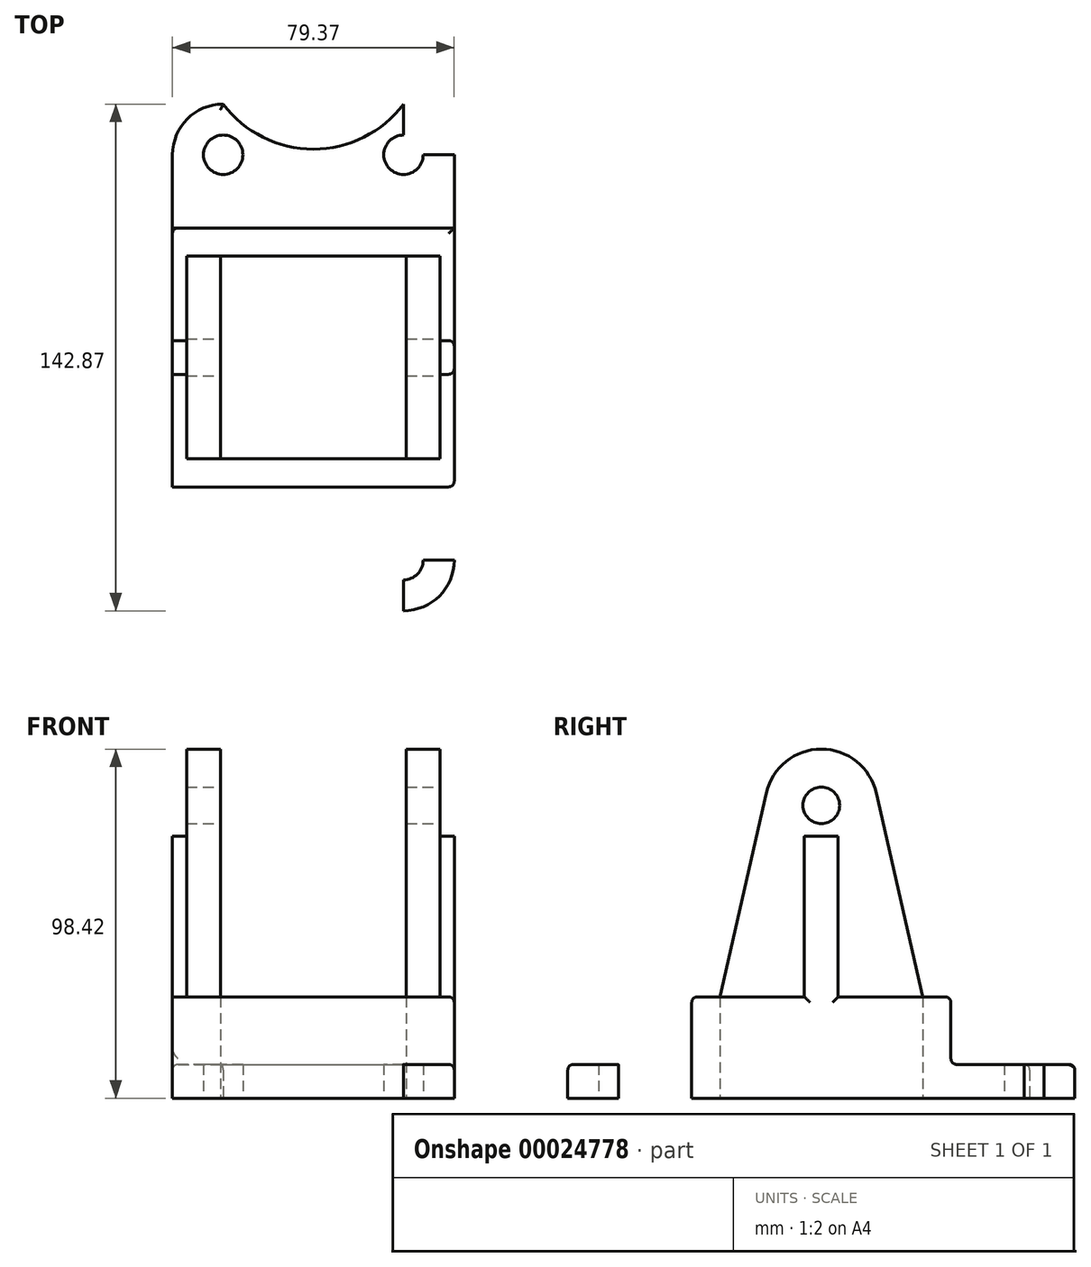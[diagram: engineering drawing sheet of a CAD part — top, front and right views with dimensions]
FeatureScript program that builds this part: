
annotation { "Feature Type Name" : "Feature", "Feature Type Description" : "" }
export const myFeature = defineFeature(function(context is Context, id is Id, definition is map)
    precondition{}
    {
        {
            var Q0;
            Q0=qCreatedBy(makeId("Top.planeOp"),FACE);
            var sketch = newSketch(context, id + "F0", { "sketchPlane" : qUnion([Q0])});
            skArc(sketch, "E0", {"start": v(-23.97, 73.31) * mm, "mid": v(-34.08, 69.13) * mm, "end": v(-38.26, 59.03) * mm});
            skLineSegment(sketch, "E1", {"start": v(-23.97, 59.03) * mm, "end": v(-23.97, 73.31) * mm, "construction": true});
            skLineSegment(sketch, "E2", {"start": v(-23.97, 59.03) * mm, "end": v(-38.26, 59.03) * mm, "construction": true});
            skLineSegment(sketch, "E3", {"start": v(-38.26, 59.03) * mm, "end": v(-38.26, -55.27) * mm});
            skLineSegment(sketch, "E4", {"start": v(-23.97, 73.31) * mm, "end": v(26.83, 73.31) * mm, "construction": true});
            skPoint(sketch, "E5", {"position": v(1.43, 73.31) * mm});
            skArc(sketch, "E6", {"start": v(-23.97, 73.31) * mm, "mid": v(1.43, 60.61) * mm, "end": v(26.83, 73.31) * mm});
            skCircle(sketch, "E7", {"center": v(-23.97, 59.03) * mm, "radius": 5.56 * mm});
            skPoint(sketch, "E8", {"position": v(-38.26, 1.88) * mm});
            skLineSegment(sketch, "E9.MirrorCS", {"start": v(-23.97, -69.56) * mm, "end": v(26.83, -69.56) * mm, "construction": true});
            skArc(sketch, "E10.MirrorCS", {"start": v(-23.97, -69.56) * mm, "mid": v(1.43, -56.86) * mm, "end": v(26.83, -69.56) * mm});
            skArc(sketch, "E11.MirrorC", {"start": v(-23.97, -69.56) * mm, "mid": v(-34.08, -65.38) * mm, "end": v(-38.26, -55.27) * mm});
            skLineSegment(sketch, "E12.MirrorCS", {"start": v(-23.97, -55.27) * mm, "end": v(-38.26, -55.27) * mm, "construction": true});
            skCircle(sketch, "E13.MirrorC", {"center": v(-23.97, -55.27) * mm, "radius": 5.56 * mm});
            skLineSegment(sketch, "E14.MirrorCS", {"start": v(-23.97, -55.27) * mm, "end": v(-23.97, -69.56) * mm, "construction": true});
            skPoint(sketch, "E15.MirrorP", {"position": v(1.43, -69.56) * mm});
            skLineSegment(sketch, "E16", {"start": v(-38.26, 1.88) * mm, "end": v(-34.3, 1.88) * mm, "construction": true});
            skLineSegment(sketch, "E17", {"start": v(-34.3, 6.64) * mm, "end": v(-34.3, -2.89) * mm});
            skPoint(sketch, "E18", {"position": v(-34.3, 1.88) * mm});
            skLineSegment(sketch, "E19", {"start": v(-34.3, 6.64) * mm, "end": v(-38.26, 6.64) * mm});
            skLineSegment(sketch, "E20", {"start": v(-34.3, -2.89) * mm, "end": v(-38.26, -2.89) * mm});
            skLineSegment(sketch, "E21", {"start": v(1.43, 73.31) * mm, "end": v(1.43, -69.56) * mm, "construction": true});
            skLineSegment(sketch, "E22", {"start": v(-34.3, 1.88) * mm, "end": v(-34.3, 30.45) * mm, "construction": true});
            skLineSegment(sketch, "E23", {"start": v(-38.26, 30.45) * mm, "end": v(1.43, 30.45) * mm});
            skLineSegment(sketch, "E24", {"start": v(-38.26, 38.39) * mm, "end": v(1.43, 38.39) * mm});
            skLineSegment(sketch, "E25.MirrorCS", {"start": v(37.14, -2.89) * mm, "end": v(41.11, -2.89) * mm});
            skLineSegment(sketch, "E26.MirrorCS", {"start": v(41.11, 1.88) * mm, "end": v(37.14, 1.88) * mm, "construction": true});
            skLineSegment(sketch, "E27.MirrorCS", {"start": v(37.14, 6.64) * mm, "end": v(37.14, -2.89) * mm});
            skLineSegment(sketch, "E28.MirrorCS", {"start": v(37.14, 6.64) * mm, "end": v(41.11, 6.64) * mm});
            skLineSegment(sketch, "E29.MirrorCS", {"start": v(37.14, 1.88) * mm, "end": v(37.14, 30.45) * mm, "construction": true});
            skCircle(sketch, "E30.MirrorC", {"center": v(26.83, -55.27) * mm, "radius": 5.56 * mm});
            skLineSegment(sketch, "E31.MirrorCS", {"start": v(26.83, -55.27) * mm, "end": v(41.11, -55.27) * mm});
            skLineSegment(sketch, "E32.MirrorCS", {"start": v(41.11, 38.39) * mm, "end": v(1.43, 38.39) * mm});
            skCircle(sketch, "E33.MirrorC", {"center": v(26.83, 59.03) * mm, "radius": 5.56 * mm});
            skArc(sketch, "E34.MirrorCS", {"start": v(26.83, -69.56) * mm, "mid": v(36.93, -65.38) * mm, "end": v(41.11, -55.27) * mm});
            skLineSegment(sketch, "E35.MirrorCS", {"start": v(41.11, 30.45) * mm, "end": v(1.43, 30.45) * mm});
            skPoint(sketch, "E36.MirrorP", {"position": v(41.11, 1.88) * mm});
            skLineSegment(sketch, "E37.MirrorCS", {"start": v(26.83, -55.27) * mm, "end": v(26.83, -69.56) * mm});
            skPoint(sketch, "E38.MirrorP", {"position": v(37.14, 1.88) * mm});
            skArc(sketch, "E39.MirrorCS", {"start": v(26.83, 73.31) * mm, "mid": v(36.93, 69.13) * mm, "end": v(41.11, 59.03) * mm});
            skLineSegment(sketch, "E40.MirrorCS", {"start": v(26.83, 59.03) * mm, "end": v(26.83, 73.31) * mm});
            skLineSegment(sketch, "E41.MirrorCS", {"start": v(26.83, 59.03) * mm, "end": v(41.11, 59.03) * mm});
            skLineSegment(sketch, "E42.MirrorCS", {"start": v(41.11, 59.03) * mm, "end": v(41.11, -55.27) * mm});
            skLineSegment(sketch, "E43", {"start": v(-34.3, -2.89) * mm, "end": v(-34.3, -26.7) * mm, "construction": true});
            skLineSegment(sketch, "E44", {"start": v(-38.26, -26.7) * mm, "end": v(41.11, -26.7) * mm});
            skLineSegment(sketch, "E45", {"start": v(-38.26, -34.64) * mm, "end": v(41.11, -34.64) * mm});
            skLineSegment(sketch, "E46", {"start": v(-34.3, 38.39) * mm, "end": v(-34.3, -34.64) * mm});
            skLineSegment(sketch, "E47", {"start": v(-24.77, 38.39) * mm, "end": v(-24.77, -34.64) * mm});
            skLineSegment(sketch, "E48", {"start": v(37.14, 38.39) * mm, "end": v(37.14, -34.64) * mm});
            skLineSegment(sketch, "E49", {"start": v(27.62, 38.39) * mm, "end": v(27.62, -34.64) * mm});
            skSolve(sketch);
        }
        {
            var Q0;
            {var subQ1=sQuery(id+"F0.wireOp",EDGE,"E23");var subQ5=sQuery(id+"F0.wireOp",EDGE,"E3");var subQ7=makeQuery(id+"F0.imprint","INTERSECT",VERTEX,{"derivedFrom":[subQ5,subQ1]});Q0=makeQuery(id+"F0.imprint","IMPRINT",FACE,{"disambiguationData":[TD([[makeQuery(id+"F0.imprint","IMPRINT",EDGE,{"disambiguationData":[TD([[subQ7,1.0]])],"derivedFrom":subQ5}),1.0]])]});}
            var Q1;
            {var subQ5=sQuery(id+"F0.wireOp",EDGE,"E19");Q1=makeQuery(id+"F0.imprint","IMPRINT",FACE,{"disambiguationData":[TD([[makeQuery(id+"F0.imprint","IMPRINT",EDGE,{"derivedFrom":subQ5}),-1.0]])]});}
            var Q2;
            {var subQ3=sQuery(id+"F0.wireOp",EDGE,"E35.MirrorCS");var subQ7=sQuery(id+"F0.wireOp",EDGE,"E23");var subQ9=makeQuery(id+"F0.imprint","INTERSECT",VERTEX,{"derivedFrom":[subQ7,subQ3]});Q2=makeQuery(id+"F0.imprint","IMPRINT",FACE,{"disambiguationData":[TD([[makeQuery(id+"F0.imprint","IMPRINT",EDGE,{"disambiguationData":[TD([[subQ9,1.0]])],"derivedFrom":subQ7}),-1.0]])]});}
            var Q3;
            {var subQ3=sQuery(id+"F0.wireOp",EDGE,"E25.MirrorCS");Q3=makeQuery(id+"F0.imprint","IMPRINT",FACE,{"disambiguationData":[TD([[makeQuery(id+"F0.imprint","IMPRINT",EDGE,{"derivedFrom":subQ3}),-1.0]])]});}
            var Q4;
            {var subQ3=sQuery(id+"F0.wireOp",EDGE,"E20");Q4=makeQuery(id+"F0.imprint","IMPRINT",FACE,{"disambiguationData":[TD([[makeQuery(id+"F0.imprint","IMPRINT",EDGE,{"derivedFrom":subQ3}),1.0]])]});}
            var Q5;
            {var subQ1=sQuery(id+"F0.wireOp",EDGE,"E44");var subQ5=sQuery(id+"F0.wireOp",EDGE,"E3");var subQ7=makeQuery(id+"F0.imprint","INTERSECT",VERTEX,{"derivedFrom":[subQ5,subQ1]});Q5=makeQuery(id+"F0.imprint","IMPRINT",FACE,{"disambiguationData":[TD([[makeQuery(id+"F0.imprint","IMPRINT",EDGE,{"disambiguationData":[TD([[subQ7,-1.0]])],"derivedFrom":subQ5}),1.0]])]});}
            var Q6;
            {var subQ3=sQuery(id+"F0.wireOp",EDGE,"E28.MirrorCS");Q6=makeQuery(id+"F0.imprint","IMPRINT",FACE,{"disambiguationData":[TD([[makeQuery(id+"F0.imprint","IMPRINT",EDGE,{"derivedFrom":subQ3}),1.0]])]});}
            var Q7;
            {var subQ0=sQuery(id+"F0.wireOp",EDGE,"E42.MirrorCS");var subQ3=sQuery(id+"F0.wireOp",EDGE,"E32.MirrorCS");var subQ4=makeQuery(id+"F0.imprint","INTERSECT",VERTEX,{"derivedFrom":[subQ3,subQ0]});Q7=makeQuery(id+"F0.imprint","IMPRINT",FACE,{"disambiguationData":[TD([[makeQuery(id+"F0.imprint","IMPRINT",EDGE,{"disambiguationData":[TD([[subQ4,-1.0]])],"derivedFrom":subQ3}),1.0]])]});}
            var Q8;
            {var subQ1=sQuery(id+"F0.wireOp",EDGE,"E44");var subQ5=sQuery(id+"F0.wireOp",EDGE,"E46");var subQ6=makeQuery(id+"F0.imprint","INTERSECT",VERTEX,{"derivedFrom":[subQ1,subQ5]});Q8=makeQuery(id+"F0.imprint","IMPRINT",FACE,{"disambiguationData":[TD([[makeQuery(id+"F0.imprint","IMPRINT",EDGE,{"disambiguationData":[TD([[subQ6,-1.0]])],"derivedFrom":subQ1}),-1.0]])]});}
            var Q9;
            {var subQ1=sQuery(id+"F0.wireOp",EDGE,"E44");var subQ5=sQuery(id+"F0.wireOp",EDGE,"E47");var subQ6=makeQuery(id+"F0.imprint","INTERSECT",VERTEX,{"derivedFrom":[subQ1,subQ5]});Q9=makeQuery(id+"F0.imprint","IMPRINT",FACE,{"disambiguationData":[TD([[makeQuery(id+"F0.imprint","IMPRINT",EDGE,{"disambiguationData":[TD([[subQ6,-1.0]])],"derivedFrom":subQ1}),-1.0]])]});}
            var Q10;
            {var subQ3=sQuery(id+"F0.wireOp",EDGE,"E32.MirrorCS");var subQ5=sQuery(id+"F0.wireOp",EDGE,"E48");var subQ7=makeQuery(id+"F0.imprint","INTERSECT",VERTEX,{"derivedFrom":[subQ3,subQ5]});Q10=makeQuery(id+"F0.imprint","IMPRINT",FACE,{"disambiguationData":[TD([[makeQuery(id+"F0.imprint","IMPRINT",EDGE,{"disambiguationData":[TD([[subQ7,-1.0]])],"derivedFrom":subQ3}),1.0]])]});}
            var Q11;
            {var subQ3=sQuery(id+"F0.wireOp",EDGE,"E42.MirrorCS");var subQ5=sQuery(id+"F0.wireOp",EDGE,"E44");var subQ7=makeQuery(id+"F0.imprint","INTERSECT",VERTEX,{"derivedFrom":[subQ3,subQ5]});Q11=makeQuery(id+"F0.imprint","IMPRINT",FACE,{"disambiguationData":[TD([[makeQuery(id+"F0.imprint","IMPRINT",EDGE,{"disambiguationData":[TD([[subQ7,-1.0]])],"derivedFrom":subQ3}),-1.0]])]});}
            var Q12;
            {var subQ0=sQuery(id+"F0.wireOp",EDGE,"E49");var subQ1=sQuery(id+"F0.wireOp",EDGE,"E44");var subQ2=makeQuery(id+"F0.imprint","INTERSECT",VERTEX,{"derivedFrom":[subQ1,subQ0]});Q12=makeQuery(id+"F0.imprint","IMPRINT",FACE,{"disambiguationData":[TD([[makeQuery(id+"F0.imprint","IMPRINT",EDGE,{"disambiguationData":[TD([[subQ2,-1.0]])],"derivedFrom":subQ1}),-1.0]])]});}
            var Q13;
            {var subQ1=sQuery(id+"F0.wireOp",EDGE,"E23");var subQ5=sQuery(id+"F0.wireOp",EDGE,"E46");var subQ6=makeQuery(id+"F0.imprint","INTERSECT",VERTEX,{"derivedFrom":[subQ1,subQ5]});Q13=makeQuery(id+"F0.imprint","IMPRINT",FACE,{"disambiguationData":[TD([[makeQuery(id+"F0.imprint","IMPRINT",EDGE,{"disambiguationData":[TD([[subQ6,-1.0]])],"derivedFrom":subQ1}),1.0]])]});}
            var Q14;
            {var subQ3=sQuery(id+"F0.wireOp",EDGE,"E35.MirrorCS");var subQ5=sQuery(id+"F0.wireOp",EDGE,"E48");var subQ9=makeQuery(id+"F0.imprint","INTERSECT",VERTEX,{"derivedFrom":[subQ3,subQ5]});Q14=makeQuery(id+"F0.imprint","IMPRINT",FACE,{"disambiguationData":[TD([[makeQuery(id+"F0.imprint","IMPRINT",EDGE,{"disambiguationData":[TD([[subQ9,-1.0]])],"derivedFrom":subQ3}),1.0]])]});}
            var Q15;
            {var subQ3=sQuery(id+"F0.wireOp",EDGE,"E23");var subQ5=sQuery(id+"F0.wireOp",EDGE,"E46");var subQ9=makeQuery(id+"F0.imprint","INTERSECT",VERTEX,{"derivedFrom":[subQ3,subQ5]});Q15=makeQuery(id+"F0.imprint","IMPRINT",FACE,{"disambiguationData":[TD([[makeQuery(id+"F0.imprint","IMPRINT",EDGE,{"disambiguationData":[TD([[subQ9,-1.0]])],"derivedFrom":subQ3}),-1.0]])]});}
            var Q16;
            {var subQ1=sQuery(id+"F0.wireOp",EDGE,"E35.MirrorCS");var subQ6=sQuery(id+"F0.wireOp",EDGE,"E23");var subQ10=makeQuery(id+"F0.imprint","INTERSECT",VERTEX,{"derivedFrom":[subQ6,subQ1]});Q16=makeQuery(id+"F0.imprint","IMPRINT",FACE,{"disambiguationData":[TD([[makeQuery(id+"F0.imprint","IMPRINT",EDGE,{"disambiguationData":[TD([[subQ10,1.0]])],"derivedFrom":subQ6}),1.0]])]});}
            var Q17;
            {var subQ19=sQuery(id+"F0.wireOp",EDGE,"E0");Q17=makeQuery(id+"F0.imprint","IMPRINT",FACE,{"disambiguationData":[TD([[makeQuery(id+"F0.imprint","IMPRINT",EDGE,{"derivedFrom":subQ19}),1.0]])]});}
            var Q18;
            {var subQ3=sQuery(id+"F0.wireOp",EDGE,"E39.MirrorCS");Q18=makeQuery(id+"F0.imprint","IMPRINT",FACE,{"disambiguationData":[TD([[makeQuery(id+"F0.imprint","IMPRINT",EDGE,{"derivedFrom":subQ3}),-1.0]])]});}
            var Q19;
            {var subQ10=sQuery(id+"F0.wireOp",EDGE,"E10.MirrorCS");Q19=makeQuery(id+"F0.imprint","IMPRINT",FACE,{"disambiguationData":[TD([[makeQuery(id+"F0.imprint","IMPRINT",EDGE,{"derivedFrom":subQ10}),1.0]])]});}
            var Q20;
            {var subQ3=sQuery(id+"F0.wireOp",EDGE,"E34.MirrorCS");Q20=makeQuery(id+"F0.imprint","IMPRINT",FACE,{"disambiguationData":[TD([[makeQuery(id+"F0.imprint","IMPRINT",EDGE,{"derivedFrom":subQ3}),1.0]])]});}
            extrude(context, id + "F1", {"entities" : qUnion([Q0, Q1, Q2, Q3, Q4, Q5, Q6, Q7, Q8, Q9, Q10, Q11, Q12, Q13, Q14, Q15, Q16, Q17, Q18, Q19, Q20]), "depth" : 9.52 * mm});
        }
        {
            var Q0;
            {var subQ0=sQuery(id+"F0.wireOp",EDGE,"E42.MirrorCS");var subQ3=sQuery(id+"F0.wireOp",EDGE,"E32.MirrorCS");var subQ4=makeQuery(id+"F0.imprint","INTERSECT",VERTEX,{"derivedFrom":[subQ3,subQ0]});Q0=makeQuery(id+"F0.imprint","IMPRINT",FACE,{"disambiguationData":[TD([[makeQuery(id+"F0.imprint","IMPRINT",EDGE,{"disambiguationData":[TD([[subQ4,-1.0]])],"derivedFrom":subQ3}),1.0]])]});}
            var Q1;
            {var subQ3=sQuery(id+"F0.wireOp",EDGE,"E32.MirrorCS");var subQ5=sQuery(id+"F0.wireOp",EDGE,"E48");var subQ7=makeQuery(id+"F0.imprint","INTERSECT",VERTEX,{"derivedFrom":[subQ3,subQ5]});Q1=makeQuery(id+"F0.imprint","IMPRINT",FACE,{"disambiguationData":[TD([[makeQuery(id+"F0.imprint","IMPRINT",EDGE,{"disambiguationData":[TD([[subQ7,-1.0]])],"derivedFrom":subQ3}),1.0]])]});}
            var Q2;
            {var subQ1=sQuery(id+"F0.wireOp",EDGE,"E35.MirrorCS");var subQ6=sQuery(id+"F0.wireOp",EDGE,"E23");var subQ10=makeQuery(id+"F0.imprint","INTERSECT",VERTEX,{"derivedFrom":[subQ6,subQ1]});Q2=makeQuery(id+"F0.imprint","IMPRINT",FACE,{"disambiguationData":[TD([[makeQuery(id+"F0.imprint","IMPRINT",EDGE,{"disambiguationData":[TD([[subQ10,1.0]])],"derivedFrom":subQ6}),1.0]])]});}
            var Q3;
            {var subQ1=sQuery(id+"F0.wireOp",EDGE,"E23");var subQ5=sQuery(id+"F0.wireOp",EDGE,"E46");var subQ6=makeQuery(id+"F0.imprint","INTERSECT",VERTEX,{"derivedFrom":[subQ1,subQ5]});Q3=makeQuery(id+"F0.imprint","IMPRINT",FACE,{"disambiguationData":[TD([[makeQuery(id+"F0.imprint","IMPRINT",EDGE,{"disambiguationData":[TD([[subQ6,-1.0]])],"derivedFrom":subQ1}),1.0]])]});}
            var Q4;
            {var subQ1=sQuery(id+"F0.wireOp",EDGE,"E23");var subQ5=sQuery(id+"F0.wireOp",EDGE,"E3");var subQ7=makeQuery(id+"F0.imprint","INTERSECT",VERTEX,{"derivedFrom":[subQ5,subQ1]});Q4=makeQuery(id+"F0.imprint","IMPRINT",FACE,{"disambiguationData":[TD([[makeQuery(id+"F0.imprint","IMPRINT",EDGE,{"disambiguationData":[TD([[subQ7,1.0]])],"derivedFrom":subQ5}),1.0]])]});}
            var Q5;
            {var subQ3=sQuery(id+"F0.wireOp",EDGE,"E42.MirrorCS");var subQ5=sQuery(id+"F0.wireOp",EDGE,"E44");var subQ7=makeQuery(id+"F0.imprint","INTERSECT",VERTEX,{"derivedFrom":[subQ3,subQ5]});Q5=makeQuery(id+"F0.imprint","IMPRINT",FACE,{"disambiguationData":[TD([[makeQuery(id+"F0.imprint","IMPRINT",EDGE,{"disambiguationData":[TD([[subQ7,-1.0]])],"derivedFrom":subQ3}),-1.0]])]});}
            var Q6;
            {var subQ0=sQuery(id+"F0.wireOp",EDGE,"E49");var subQ1=sQuery(id+"F0.wireOp",EDGE,"E44");var subQ2=makeQuery(id+"F0.imprint","INTERSECT",VERTEX,{"derivedFrom":[subQ1,subQ0]});Q6=makeQuery(id+"F0.imprint","IMPRINT",FACE,{"disambiguationData":[TD([[makeQuery(id+"F0.imprint","IMPRINT",EDGE,{"disambiguationData":[TD([[subQ2,-1.0]])],"derivedFrom":subQ1}),-1.0]])]});}
            var Q7;
            {var subQ1=sQuery(id+"F0.wireOp",EDGE,"E44");var subQ5=sQuery(id+"F0.wireOp",EDGE,"E47");var subQ6=makeQuery(id+"F0.imprint","INTERSECT",VERTEX,{"derivedFrom":[subQ1,subQ5]});Q7=makeQuery(id+"F0.imprint","IMPRINT",FACE,{"disambiguationData":[TD([[makeQuery(id+"F0.imprint","IMPRINT",EDGE,{"disambiguationData":[TD([[subQ6,-1.0]])],"derivedFrom":subQ1}),-1.0]])]});}
            var Q8;
            {var subQ1=sQuery(id+"F0.wireOp",EDGE,"E44");var subQ5=sQuery(id+"F0.wireOp",EDGE,"E46");var subQ6=makeQuery(id+"F0.imprint","INTERSECT",VERTEX,{"derivedFrom":[subQ1,subQ5]});Q8=makeQuery(id+"F0.imprint","IMPRINT",FACE,{"disambiguationData":[TD([[makeQuery(id+"F0.imprint","IMPRINT",EDGE,{"disambiguationData":[TD([[subQ6,-1.0]])],"derivedFrom":subQ1}),-1.0]])]});}
            var Q9;
            {var subQ1=sQuery(id+"F0.wireOp",EDGE,"E44");var subQ5=sQuery(id+"F0.wireOp",EDGE,"E3");var subQ7=makeQuery(id+"F0.imprint","INTERSECT",VERTEX,{"derivedFrom":[subQ5,subQ1]});Q9=makeQuery(id+"F0.imprint","IMPRINT",FACE,{"disambiguationData":[TD([[makeQuery(id+"F0.imprint","IMPRINT",EDGE,{"disambiguationData":[TD([[subQ7,-1.0]])],"derivedFrom":subQ5}),1.0]])]});}
            var Q10;
            {var subQ5=sQuery(id+"F0.wireOp",EDGE,"E19");Q10=makeQuery(id+"F0.imprint","IMPRINT",FACE,{"disambiguationData":[TD([[makeQuery(id+"F0.imprint","IMPRINT",EDGE,{"derivedFrom":subQ5}),-1.0]])]});}
            var Q11;
            {var subQ3=sQuery(id+"F0.wireOp",EDGE,"E20");Q11=makeQuery(id+"F0.imprint","IMPRINT",FACE,{"disambiguationData":[TD([[makeQuery(id+"F0.imprint","IMPRINT",EDGE,{"derivedFrom":subQ3}),1.0]])]});}
            var Q12;
            {var subQ3=sQuery(id+"F0.wireOp",EDGE,"E28.MirrorCS");Q12=makeQuery(id+"F0.imprint","IMPRINT",FACE,{"disambiguationData":[TD([[makeQuery(id+"F0.imprint","IMPRINT",EDGE,{"derivedFrom":subQ3}),1.0]])]});}
            var Q13;
            {var subQ3=sQuery(id+"F0.wireOp",EDGE,"E25.MirrorCS");Q13=makeQuery(id+"F0.imprint","IMPRINT",FACE,{"disambiguationData":[TD([[makeQuery(id+"F0.imprint","IMPRINT",EDGE,{"derivedFrom":subQ3}),-1.0]])]});}
            var Q14;
            {var subQ3=sQuery(id+"F0.wireOp",EDGE,"E35.MirrorCS");var subQ5=sQuery(id+"F0.wireOp",EDGE,"E48");var subQ9=makeQuery(id+"F0.imprint","INTERSECT",VERTEX,{"derivedFrom":[subQ3,subQ5]});Q14=makeQuery(id+"F0.imprint","IMPRINT",FACE,{"disambiguationData":[TD([[makeQuery(id+"F0.imprint","IMPRINT",EDGE,{"disambiguationData":[TD([[subQ9,-1.0]])],"derivedFrom":subQ3}),1.0]])]});}
            var Q15;
            {var subQ3=sQuery(id+"F0.wireOp",EDGE,"E23");var subQ5=sQuery(id+"F0.wireOp",EDGE,"E46");var subQ9=makeQuery(id+"F0.imprint","INTERSECT",VERTEX,{"derivedFrom":[subQ3,subQ5]});Q15=makeQuery(id+"F0.imprint","IMPRINT",FACE,{"disambiguationData":[TD([[makeQuery(id+"F0.imprint","IMPRINT",EDGE,{"disambiguationData":[TD([[subQ9,-1.0]])],"derivedFrom":subQ3}),-1.0]])]});}
            extrude(context, id + "F2", {"entities" : qUnion([Q0, Q1, Q2, Q3, Q4, Q5, Q6, Q7, Q8, Q9, Q10, Q11, Q12, Q13, Q14, Q15]), "operationType" : NewBodyOperationType.ADD, "depth" : 28.57 * mm});
        }
        {
            var Q0;
            Q0=makeQuery(id+"F2.boolean.opBoolean","SPLIT",FACE,{"disambiguationData":[TD([makeQuery(id+"F2.opExtrude","SWEPT_FACE",FACE,{"disambiguationData":[OSD([sQuery(id+"F0.wireOp",EDGE,"E44")])]})])],"derivedFrom":makeQuery(id+"F1.opExtrude","CAP_FACE",FACE,{"disambiguationData":[OSD([sQuery(id+"F0.wireOp",EDGE,"E0"),sQuery(id+"F0.wireOp",EDGE,"E3"),sQuery(id+"F0.wireOp",EDGE,"E6"),sQuery(id+"F0.wireOp",EDGE,"E7"),sQuery(id+"F0.wireOp",EDGE,"E10.MirrorCS"),sQuery(id+"F0.wireOp",EDGE,"E11.MirrorC"),sQuery(id+"F0.wireOp",EDGE,"E13.MirrorC"),sQuery(id+"F0.wireOp",EDGE,"E30.MirrorC"),sQuery(id+"F0.wireOp",EDGE,"E33.MirrorC"),sQuery(id+"F0.wireOp",EDGE,"E34.MirrorCS"),sQuery(id+"F0.wireOp",EDGE,"E39.MirrorCS"),sQuery(id+"F0.wireOp",EDGE,"E42.MirrorCS")])],"isStart":false})});
            extrude(context, id + "F3", {"entities" : qUnion([Q0]), "operationType" : NewBodyOperationType.REMOVE, "oppositeDirection" : true, "depth" : 25.4 * mm});
        }
        {
            var Q0;
            {var subQ2=sQuery(id+"F0.wireOp",EDGE,"E19");Q0=makeQuery(id+"F0.imprint","IMPRINT",FACE,{"disambiguationData":[TD([[makeQuery(id+"F0.imprint","IMPRINT",EDGE,{"derivedFrom":subQ2}),1.0]])]});}
            var Q1;
            {var subQ2=sQuery(id+"F0.wireOp",EDGE,"E25.MirrorCS");Q1=makeQuery(id+"F0.imprint","IMPRINT",FACE,{"disambiguationData":[TD([[makeQuery(id+"F0.imprint","IMPRINT",EDGE,{"derivedFrom":subQ2}),1.0]])]});}
            extrude(context, id + "F4", {"entities" : qUnion([Q0, Q1]), "operationType" : NewBodyOperationType.ADD, "depth" : 73.82 * mm});
        }
        {
            var Q0;
            Q0=makeQuery(id+"F2.opExtrude","CAP_FACE",FACE,{"disambiguationData":[OSD([sQuery(id+"F0.wireOp",EDGE,"E3"),sQuery(id+"F0.wireOp",EDGE,"E19"),sQuery(id+"F0.wireOp",EDGE,"E20"),sQuery(id+"F0.wireOp",EDGE,"E23"),sQuery(id+"F0.wireOp",EDGE,"E24"),sQuery(id+"F0.wireOp",EDGE,"E25.MirrorCS"),sQuery(id+"F0.wireOp",EDGE,"E28.MirrorCS"),sQuery(id+"F0.wireOp",EDGE,"E32.MirrorCS"),sQuery(id+"F0.wireOp",EDGE,"E35.MirrorCS"),sQuery(id+"F0.wireOp",EDGE,"E42.MirrorCS"),sQuery(id+"F0.wireOp",EDGE,"E44"),sQuery(id+"F0.wireOp",EDGE,"E45"),sQuery(id+"F0.wireOp",EDGE,"E46"),sQuery(id+"F0.wireOp",EDGE,"E47"),sQuery(id+"F0.wireOp",EDGE,"E48"),sQuery(id+"F0.wireOp",EDGE,"E49")])],"isStart":false});
            cPlane(context, id + "F5", {"entities" : qUnion([Q0]), "cplaneType" : CPlaneType.OFFSET, "offset" : 0 * mm, "width" : 152.4 * mm, "height" : 152.4 * mm});
        }
        {
            var Q0;
            Q0=qCreatedBy(id+"F5.planeOp",FACE);
            var sketch = newSketch(context, id + "F6", { "sketchPlane" : qUnion([Q0])});
            skLineSegment(sketch, "E50.0.0", {"start": v(37.14, 6.64) * mm, "end": v(37.14, 30.45) * mm});
            skLineSegment(sketch, "E50.0.1", {"start": v(37.14, 30.45) * mm, "end": v(27.62, 30.45) * mm});
            skLineSegment(sketch, "E50.0.2", {"start": v(27.62, 30.45) * mm, "end": v(27.62, -26.7) * mm});
            skLineSegment(sketch, "E50.0.3", {"start": v(27.62, -26.7) * mm, "end": v(37.14, -26.7) * mm});
            skLineSegment(sketch, "E50.0.4", {"start": v(37.14, -26.7) * mm, "end": v(37.14, -2.89) * mm});
            skLineSegment(sketch, "E50.0.5", {"start": v(37.14, -2.89) * mm, "end": v(37.14, 6.64) * mm});
            skLineSegment(sketch, "E51.0.0", {"start": v(-24.77, 30.45) * mm, "end": v(-34.3, 30.45) * mm});
            skLineSegment(sketch, "E51.0.1", {"start": v(-34.3, 30.45) * mm, "end": v(-34.3, 6.64) * mm});
            skLineSegment(sketch, "E51.0.2", {"start": v(-34.3, 6.64) * mm, "end": v(-34.3, -2.89) * mm});
            skLineSegment(sketch, "E51.0.3", {"start": v(-34.3, -2.89) * mm, "end": v(-34.3, -26.7) * mm});
            skLineSegment(sketch, "E51.0.4", {"start": v(-34.3, -26.7) * mm, "end": v(-24.77, -26.7) * mm});
            skLineSegment(sketch, "E51.0.5", {"start": v(-24.77, -26.7) * mm, "end": v(-24.77, 30.45) * mm});
            skSolve(sketch);
        }
        {
            var Q0;
            Q0=makeQuery(id+"F6.imprint","IMPRINT",FACE,{"disambiguationData":[TD([[makeQuery(id+"F6.imprint","IMPRINT",EDGE,{"derivedFrom":sQuery(id+"F6.wireOp",EDGE,"E51.0.0")}),1.0]])]});
            var Q1;
            Q1=makeQuery(id+"F6.imprint","IMPRINT",FACE,{"disambiguationData":[TD([[makeQuery(id+"F6.imprint","IMPRINT",EDGE,{"derivedFrom":sQuery(id+"F6.wireOp",EDGE,"E50.0.0")}),1.0]])]});
            extrude(context, id + "F7", {"entities" : qUnion([Q0, Q1]), "operationType" : NewBodyOperationType.ADD, "depth" : 69.85 * mm});
        }
        {
            var Q0;
            Q0=makeQuery(id+"F7.opExtrude","SWEPT_FACE",FACE,{"disambiguationData":[OSD([sQuery(id+"F6.wireOp",EDGE,"E50.0.0"),sQuery(id+"F6.wireOp",EDGE,"E50.0.4"),sQuery(id+"F6.wireOp",EDGE,"E50.0.5")])]});
            cPlane(context, id + "F8", {"entities" : qUnion([Q0]), "cplaneType" : CPlaneType.OFFSET, "offset" : 0 * mm, "width" : 152.4 * mm, "height" : 152.4 * mm});
        }
        {
            var Q0;
            Q0=qCreatedBy(id+"F8.planeOp",FACE);
            var sketch = newSketch(context, id + "F9", { "sketchPlane" : qUnion([Q0])});
            skLineSegment(sketch, "E52.0", {"start": v(-2.89, 28.58) * mm, "end": v(-34.64, 28.58) * mm});
            skLineSegment(sketch, "E53.0", {"start": v(38.39, 28.58) * mm, "end": v(6.64, 28.58) * mm});
            skLineSegment(sketch, "E54.0.0", {"start": v(-26.7, 28.58) * mm, "end": v(-2.89, 28.58) * mm});
            skLineSegment(sketch, "E54.0.1", {"start": v(-2.89, 28.58) * mm, "end": v(-2.89, 73.82) * mm});
            skLineSegment(sketch, "E54.0.2", {"start": v(-2.89, 73.82) * mm, "end": v(6.64, 73.82) * mm});
            skLineSegment(sketch, "E54.0.3", {"start": v(6.64, 73.82) * mm, "end": v(6.64, 28.58) * mm});
            skLineSegment(sketch, "E54.0.4", {"start": v(6.64, 28.58) * mm, "end": v(30.45, 28.58) * mm});
            skLineSegment(sketch, "E54.0.5", {"start": v(30.45, 28.58) * mm, "end": v(30.45, 98.43) * mm});
            skLineSegment(sketch, "E54.0.6", {"start": v(30.45, 98.43) * mm, "end": v(-26.7, 98.43) * mm});
            skLineSegment(sketch, "E54.0.7", {"start": v(-26.7, 98.43) * mm, "end": v(-26.7, 28.58) * mm});
            skLineSegment(sketch, "E55", {"start": v(-2.89, 28.58) * mm, "end": v(6.64, 28.58) * mm});
            skPoint(sketch, "E56", {"position": v(1.88, 28.58) * mm});
            skCircle(sketch, "E57", {"center": v(1.88, 82.55) * mm, "radius": 5.16 * mm});
            skLineSegment(sketch, "E58", {"start": v(-26.7, 28.57) * mm, "end": v(-13.6, 86.08) * mm});
            skLineSegment(sketch, "E59", {"start": v(30.45, 28.58) * mm, "end": v(17.35, 86.08) * mm});
            skArc(sketch, "E60.trimOffspring", {"start": v(17.35, 86.08) * mm, "mid": v(1.88, 98.43) * mm, "end": v(-13.6, 86.08) * mm});
            skLineSegment(sketch, "E61", {"start": v(-26.7, 28.58) * mm, "end": v(-26.7, 98.43) * mm});
            skLineSegment(sketch, "E62", {"start": v(-26.7, 98.43) * mm, "end": v(30.45, 98.43) * mm});
            skSolve(sketch);
        }
        {
            var Q0;
            {var subQ4=sQuery(id+"F9.wireOp",EDGE,"E58");Q0=makeQuery(id+"F9.imprint","IMPRINT",FACE,{"disambiguationData":[TD([[makeQuery(id+"F9.imprint","IMPRINT",EDGE,{"derivedFrom":subQ4}),1.0]])]});}
            var Q1;
            {var subQ4=sQuery(id+"F9.wireOp",EDGE,"E59");Q1=makeQuery(id+"F9.imprint","IMPRINT",FACE,{"disambiguationData":[TD([[makeQuery(id+"F9.imprint","IMPRINT",EDGE,{"derivedFrom":subQ4}),-1.0]])]});}
            var Q2;
            Q2=makeQuery(id+"F9.imprint","IMPRINT",FACE,{"disambiguationData":[TD([[makeQuery(id+"F9.imprint","IMPRINT",EDGE,{"derivedFrom":sQuery(id+"F9.wireOp",EDGE,"E57")}),1.0]])]});
            extrude(context, id + "F10", {"entities" : qUnion([Q0, Q1, Q2]), "operationType" : NewBodyOperationType.REMOVE, "oppositeDirection" : true, "depth" : 101.6 * mm});
        }
        {
            var Q0;
            Q0=makeQuery(id+"F2.opExtrude","CAP_EDGE",EDGE,{"disambiguationData":[OSD([sQuery(id+"F0.wireOp",EDGE,"E24"),sQuery(id+"F0.wireOp",EDGE,"E32.MirrorCS")])],"isStart":false});
            var Q1;
            Q1=makeQuery(id+"F4.opExtrude","SWEPT_EDGE",EDGE,{"disambiguationData":[OSD([sQuery(id+"F0.wireOp",EDGE,"E28.MirrorCS"),sQuery(id+"F0.wireOp",EDGE,"E48")])]});
            var Q2;
            {var subQ0=sQuery(id+"F6.wireOp",EDGE,"E50.0.0");var subQ1=sQuery(id+"F6.wireOp",EDGE,"E50.0.4");var subQ2=sQuery(id+"F6.wireOp",EDGE,"E50.0.5");var subQ3=sQuery(id+"F0.wireOp",EDGE,"E25.MirrorCS");Q2=makeQuery(id+"F7.boolean.opBoolean","SPLIT",EDGE,{"disambiguationData":[TD([makeQuery(id+"F4.opExtrude","SWEPT_FACE",FACE,{"disambiguationData":[OSD([subQ3])]})])],"derivedFrom":makeQuery(id+"F7.opExtrude","CAP_EDGE",EDGE,{"disambiguationData":[OSD([subQ0,subQ1,subQ2])],"isStart":true})});}
            var Q3;
            Q3=makeQuery(id+"F1.opExtrude","CAP_EDGE",EDGE,{"disambiguationData":[OSD([sQuery(id+"F0.wireOp",EDGE,"E10.MirrorCS")])],"isStart":false});
            var Q4;
            {var subQ0=sQuery(id+"F6.wireOp",EDGE,"E50.0.0");var subQ1=sQuery(id+"F6.wireOp",EDGE,"E50.0.4");var subQ2=sQuery(id+"F6.wireOp",EDGE,"E50.0.5");var subQ3=sQuery(id+"F0.wireOp",EDGE,"E28.MirrorCS");Q4=makeQuery(id+"F7.boolean.opBoolean","SPLIT",EDGE,{"disambiguationData":[TD([makeQuery(id+"F4.opExtrude","SWEPT_FACE",FACE,{"disambiguationData":[OSD([subQ3])]})])],"derivedFrom":makeQuery(id+"F7.opExtrude","CAP_EDGE",EDGE,{"disambiguationData":[OSD([subQ0,subQ1,subQ2])],"isStart":true})});}
            var Q5;
            Q5=makeQuery(id+"F1.opExtrude","CAP_EDGE",EDGE,{"disambiguationData":[OSD([sQuery(id+"F0.wireOp",EDGE,"E34.MirrorCS")])],"isStart":false});
            var Q6;
            Q6=makeQuery(id+"F1.opExtrude","CAP_EDGE",EDGE,{"disambiguationData":[OSD([sQuery(id+"F0.wireOp",EDGE,"E11.MirrorC")])],"isStart":false});
            var Q7;
            {var subQ0=sQuery(id+"F0.wireOp",EDGE,"E49");var subQ1=sQuery(id+"F9.wireOp",EDGE,"E60.trimOffspring");Q7=makeQuery(id+"F10.boolean.opBoolean","INTERSECT",EDGE,{"derivedFrom":[makeQuery(id+"F7.boolean.opBoolean","MERGE",FACE,{"derivedFrom":[makeQuery(id+"F3.boolean.opBoolean","MERGE",FACE,{"derivedFrom":[makeQuery(id+"F2.opExtrude","SWEPT_FACE",FACE,{"disambiguationData":[OSD([subQ0])]}),makeQuery(id+"F3.opExtrude","SWEPT_FACE",FACE,{"disambiguationData":[OSD([sQuery(id+"F0.wireOp",EDGE,"E0"),sQuery(id+"F0.wireOp",EDGE,"E3"),sQuery(id+"F0.wireOp",EDGE,"E6"),sQuery(id+"F0.wireOp",EDGE,"E7"),sQuery(id+"F0.wireOp",EDGE,"E10.MirrorCS"),sQuery(id+"F0.wireOp",EDGE,"E11.MirrorC"),sQuery(id+"F0.wireOp",EDGE,"E13.MirrorC"),sQuery(id+"F0.wireOp",EDGE,"E19"),sQuery(id+"F0.wireOp",EDGE,"E20"),sQuery(id+"F0.wireOp",EDGE,"E25.MirrorCS"),sQuery(id+"F0.wireOp",EDGE,"E28.MirrorCS"),sQuery(id+"F0.wireOp",EDGE,"E30.MirrorC"),sQuery(id+"F0.wireOp",EDGE,"E33.MirrorC"),sQuery(id+"F0.wireOp",EDGE,"E34.MirrorCS"),sQuery(id+"F0.wireOp",EDGE,"E39.MirrorCS"),sQuery(id+"F0.wireOp",EDGE,"E42.MirrorCS"),sQuery(id+"F0.wireOp",EDGE,"E46"),sQuery(id+"F0.wireOp",EDGE,"E48"),subQ0])]})]}),makeQuery(id+"F7.opExtrude","SWEPT_FACE",FACE,{"disambiguationData":[OSD([sQuery(id+"F6.wireOp",EDGE,"E50.0.2")])]})]}),makeQuery(id+"F10.opExtrude","SWEPT_FACE",FACE,{"disambiguationData":[OSD([subQ1]),TDD([makeQuery(id+"F9.imprint","IMPRINT",EDGE,{"disambiguationData":[TD([[makeQuery(id+"F9.imprint","INTERSECT",VERTEX,{"derivedFrom":[sQuery(id+"F9.wireOp",EDGE,"E59"),subQ1]}),-1.0]])],"derivedFrom":subQ1})])]}),makeQuery(id+"F10.opExtrude","SWEPT_FACE",FACE,{"disambiguationData":[OSD([subQ1]),TDD([makeQuery(id+"F9.imprint","IMPRINT",EDGE,{"disambiguationData":[TD([[makeQuery(id+"F9.imprint","INTERSECT",VERTEX,{"derivedFrom":[sQuery(id+"F9.wireOp",EDGE,"E58"),subQ1]}),1.0]])],"derivedFrom":subQ1})])]})]});}
            var Q8;
            {var subQ0=sQuery(id+"F0.wireOp",EDGE,"E47");Q8=makeQuery(id+"F10.boolean.opBoolean","INTERSECT",EDGE,{"derivedFrom":[makeQuery(id+"F7.boolean.opBoolean","MERGE",FACE,{"derivedFrom":[makeQuery(id+"F3.boolean.opBoolean","MERGE",FACE,{"derivedFrom":[makeQuery(id+"F2.opExtrude","SWEPT_FACE",FACE,{"disambiguationData":[OSD([subQ0])]}),makeQuery(id+"F3.opExtrude","SWEPT_FACE",FACE,{"disambiguationData":[OSD([sQuery(id+"F0.wireOp",EDGE,"E0"),sQuery(id+"F0.wireOp",EDGE,"E3"),sQuery(id+"F0.wireOp",EDGE,"E6"),sQuery(id+"F0.wireOp",EDGE,"E7"),sQuery(id+"F0.wireOp",EDGE,"E10.MirrorCS"),sQuery(id+"F0.wireOp",EDGE,"E11.MirrorC"),sQuery(id+"F0.wireOp",EDGE,"E13.MirrorC"),sQuery(id+"F0.wireOp",EDGE,"E19"),sQuery(id+"F0.wireOp",EDGE,"E20"),sQuery(id+"F0.wireOp",EDGE,"E25.MirrorCS"),sQuery(id+"F0.wireOp",EDGE,"E28.MirrorCS"),sQuery(id+"F0.wireOp",EDGE,"E30.MirrorC"),sQuery(id+"F0.wireOp",EDGE,"E33.MirrorC"),sQuery(id+"F0.wireOp",EDGE,"E34.MirrorCS"),sQuery(id+"F0.wireOp",EDGE,"E39.MirrorCS"),sQuery(id+"F0.wireOp",EDGE,"E42.MirrorCS"),sQuery(id+"F0.wireOp",EDGE,"E46"),subQ0,sQuery(id+"F0.wireOp",EDGE,"E48")])]})]}),makeQuery(id+"F7.opExtrude","SWEPT_FACE",FACE,{"disambiguationData":[OSD([sQuery(id+"F6.wireOp",EDGE,"E51.0.5")])]})]}),makeQuery(id+"F10.opExtrude","SWEPT_FACE",FACE,{"disambiguationData":[OSD([sQuery(id+"F9.wireOp",EDGE,"E59")])]})]});}
            var Q9;
            {var subQ0=sQuery(id+"F0.wireOp",EDGE,"E49");Q9=makeQuery(id+"F10.boolean.opBoolean","INTERSECT",EDGE,{"derivedFrom":[makeQuery(id+"F7.boolean.opBoolean","MERGE",FACE,{"derivedFrom":[makeQuery(id+"F3.boolean.opBoolean","MERGE",FACE,{"derivedFrom":[makeQuery(id+"F2.opExtrude","SWEPT_FACE",FACE,{"disambiguationData":[OSD([subQ0])]}),makeQuery(id+"F3.opExtrude","SWEPT_FACE",FACE,{"disambiguationData":[OSD([sQuery(id+"F0.wireOp",EDGE,"E0"),sQuery(id+"F0.wireOp",EDGE,"E3"),sQuery(id+"F0.wireOp",EDGE,"E6"),sQuery(id+"F0.wireOp",EDGE,"E7"),sQuery(id+"F0.wireOp",EDGE,"E10.MirrorCS"),sQuery(id+"F0.wireOp",EDGE,"E11.MirrorC"),sQuery(id+"F0.wireOp",EDGE,"E13.MirrorC"),sQuery(id+"F0.wireOp",EDGE,"E19"),sQuery(id+"F0.wireOp",EDGE,"E20"),sQuery(id+"F0.wireOp",EDGE,"E25.MirrorCS"),sQuery(id+"F0.wireOp",EDGE,"E28.MirrorCS"),sQuery(id+"F0.wireOp",EDGE,"E30.MirrorC"),sQuery(id+"F0.wireOp",EDGE,"E33.MirrorC"),sQuery(id+"F0.wireOp",EDGE,"E34.MirrorCS"),sQuery(id+"F0.wireOp",EDGE,"E39.MirrorCS"),sQuery(id+"F0.wireOp",EDGE,"E42.MirrorCS"),sQuery(id+"F0.wireOp",EDGE,"E46"),sQuery(id+"F0.wireOp",EDGE,"E48"),subQ0])]})]}),makeQuery(id+"F7.opExtrude","SWEPT_FACE",FACE,{"disambiguationData":[OSD([sQuery(id+"F6.wireOp",EDGE,"E50.0.2")])]})]}),makeQuery(id+"F10.opExtrude","SWEPT_FACE",FACE,{"disambiguationData":[OSD([sQuery(id+"F9.wireOp",EDGE,"E59")])]})]});}
            var Q10;
            Q10=makeQuery(id+"F2.opExtrude","CAP_EDGE",EDGE,{"disambiguationData":[OSD([sQuery(id+"F0.wireOp",EDGE,"E44")])],"isStart":false});
            var Q11;
            Q11=makeQuery(id+"F10.boolean.opBoolean","MERGE",EDGE,{"derivedFrom":[makeQuery(id+"F7.opExtrude","CAP_EDGE",EDGE,{"disambiguationData":[OSD([sQuery(id+"F6.wireOp",EDGE,"E50.0.1")])],"isStart":true}),makeQuery(id+"F10.opExtrude","SWEPT_EDGE",EDGE,{"disambiguationData":[OSD([sQuery(id+"F9.wireOp",EDGE,"E54.0.4"),sQuery(id+"F9.wireOp",EDGE,"E59"),sQuery(id+"F9.wireOp",EDGE,"E54.0.5")])]})]});
            var Q12;
            Q12=makeQuery(id+"F10.boolean.opBoolean","MERGE",EDGE,{"derivedFrom":[makeQuery(id+"F7.opExtrude","CAP_EDGE",EDGE,{"disambiguationData":[OSD([sQuery(id+"F6.wireOp",EDGE,"E50.0.3")])],"isStart":true}),makeQuery(id+"F10.opExtrude","SWEPT_EDGE",EDGE,{"disambiguationData":[OSD([sQuery(id+"F9.wireOp",EDGE,"E54.0.0"),sQuery(id+"F9.wireOp",EDGE,"E58"),sQuery(id+"F9.wireOp",EDGE,"E61")])]})]});
            var Q13;
            {var subQ0=sQuery(id+"F9.wireOp",EDGE,"E60.trimOffspring");Q13=makeQuery(id+"F10.boolean.opBoolean","TWEAK_EDGE",EDGE,{"derivedFrom":[makeQuery(id+"F10.opExtrude","CAP_EDGE",EDGE,{"disambiguationData":[OSD([subQ0]),TDD([makeQuery(id+"F9.imprint","IMPRINT",EDGE,{"disambiguationData":[TD([[makeQuery(id+"F9.imprint","INTERSECT",VERTEX,{"derivedFrom":[sQuery(id+"F9.wireOp",EDGE,"E59"),subQ0]}),-1.0]])],"derivedFrom":subQ0})])],"isStart":true}),makeQuery(id+"F10.opExtrude","CAP_EDGE",EDGE,{"disambiguationData":[OSD([subQ0]),TDD([makeQuery(id+"F9.imprint","IMPRINT",EDGE,{"disambiguationData":[TD([[makeQuery(id+"F9.imprint","INTERSECT",VERTEX,{"derivedFrom":[sQuery(id+"F9.wireOp",EDGE,"E58"),subQ0]}),1.0]])],"derivedFrom":subQ0})])],"isStart":true})]});}
            var Q14;
            Q14=makeQuery(id+"F10.boolean.opBoolean","COPY",EDGE,{"derivedFrom":makeQuery(id+"F10.opExtrude","CAP_EDGE",EDGE,{"disambiguationData":[OSD([sQuery(id+"F9.wireOp",EDGE,"E58")])],"isStart":true})});
            var Q15;
            Q15=makeQuery(id+"F10.boolean.opBoolean","COPY",EDGE,{"derivedFrom":makeQuery(id+"F10.opExtrude","CAP_EDGE",EDGE,{"disambiguationData":[OSD([sQuery(id+"F9.wireOp",EDGE,"E59")])],"isStart":true})});
            var Q16;
            {var subQ0=sQuery(id+"F0.wireOp",EDGE,"E3");var subQ1=makeQuery(id+"F0.imprint","INTERSECT",VERTEX,{"derivedFrom":[subQ0,sQuery(id+"F0.wireOp",EDGE,"E23")]});Q16=makeQuery(id+"F2.opExtrude","CAP_EDGE",EDGE,{"disambiguationData":[OSD([subQ0]),TDD([makeQuery(id+"F0.imprint","IMPRINT",EDGE,{"disambiguationData":[TD([[subQ1,1.0]])],"derivedFrom":subQ0}),makeQuery(id+"F0.imprint","IMPRINT",EDGE,{"disambiguationData":[TD([[makeQuery(id+"F0.imprint","INTERSECT",VERTEX,{"derivedFrom":[subQ0,sQuery(id+"F0.wireOp",EDGE,"E19")]}),1.0]])],"derivedFrom":subQ0})])],"isStart":false});}
            var Q17;
            {var subQ0=sQuery(id+"F9.wireOp",EDGE,"E60.trimOffspring");Q17=makeQuery(id+"F10.boolean.opBoolean","INTERSECT",EDGE,{"derivedFrom":[makeQuery(id+"F7.opExtrude","SWEPT_FACE",FACE,{"disambiguationData":[OSD([sQuery(id+"F6.wireOp",EDGE,"E51.0.1"),sQuery(id+"F6.wireOp",EDGE,"E51.0.2"),sQuery(id+"F6.wireOp",EDGE,"E51.0.3")])]}),makeQuery(id+"F10.opExtrude","SWEPT_FACE",FACE,{"disambiguationData":[OSD([subQ0]),TDD([makeQuery(id+"F9.imprint","IMPRINT",EDGE,{"disambiguationData":[TD([[makeQuery(id+"F9.imprint","INTERSECT",VERTEX,{"derivedFrom":[sQuery(id+"F9.wireOp",EDGE,"E59"),subQ0]}),-1.0]])],"derivedFrom":subQ0})])]}),makeQuery(id+"F10.opExtrude","SWEPT_FACE",FACE,{"disambiguationData":[OSD([subQ0]),TDD([makeQuery(id+"F9.imprint","IMPRINT",EDGE,{"disambiguationData":[TD([[makeQuery(id+"F9.imprint","INTERSECT",VERTEX,{"derivedFrom":[sQuery(id+"F9.wireOp",EDGE,"E58"),subQ0]}),1.0]])],"derivedFrom":subQ0})])]})]});}
            var Q18;
            Q18=makeQuery(id+"F1.opExtrude","CAP_EDGE",EDGE,{"disambiguationData":[OSD([sQuery(id+"F0.wireOp",EDGE,"E39.MirrorCS")])],"isStart":false});
            var Q19;
            Q19=makeQuery(id+"F10.boolean.opBoolean","COPY",EDGE,{"disambiguationData":[OD(0.0)],"derivedFrom":makeQuery(id+"F10.opExtrude","SWEPT_EDGE",EDGE,{"disambiguationData":[OSD([sQuery(id+"F9.wireOp",EDGE,"E58"),sQuery(id+"F9.wireOp",EDGE,"E60.trimOffspring")])]})});
            var Q20;
            Q20=makeQuery(id+"F4.opExtrude","CAP_EDGE",EDGE,{"disambiguationData":[OSD([sQuery(id+"F0.wireOp",EDGE,"E28.MirrorCS")])],"isStart":false});
            var Q21;
            Q21=makeQuery(id+"F2.opExtrude","CAP_EDGE",EDGE,{"disambiguationData":[OSD([sQuery(id+"F0.wireOp",EDGE,"E45")])],"isStart":false});
            var Q22;
            {var subQ0=sQuery(id+"F0.wireOp",EDGE,"E49");Q22=makeQuery(id+"F10.boolean.opBoolean","INTERSECT",EDGE,{"derivedFrom":[makeQuery(id+"F7.boolean.opBoolean","MERGE",FACE,{"derivedFrom":[makeQuery(id+"F3.boolean.opBoolean","MERGE",FACE,{"derivedFrom":[makeQuery(id+"F2.opExtrude","SWEPT_FACE",FACE,{"disambiguationData":[OSD([subQ0])]}),makeQuery(id+"F3.opExtrude","SWEPT_FACE",FACE,{"disambiguationData":[OSD([sQuery(id+"F0.wireOp",EDGE,"E0"),sQuery(id+"F0.wireOp",EDGE,"E3"),sQuery(id+"F0.wireOp",EDGE,"E6"),sQuery(id+"F0.wireOp",EDGE,"E7"),sQuery(id+"F0.wireOp",EDGE,"E10.MirrorCS"),sQuery(id+"F0.wireOp",EDGE,"E11.MirrorC"),sQuery(id+"F0.wireOp",EDGE,"E13.MirrorC"),sQuery(id+"F0.wireOp",EDGE,"E19"),sQuery(id+"F0.wireOp",EDGE,"E20"),sQuery(id+"F0.wireOp",EDGE,"E25.MirrorCS"),sQuery(id+"F0.wireOp",EDGE,"E28.MirrorCS"),sQuery(id+"F0.wireOp",EDGE,"E30.MirrorC"),sQuery(id+"F0.wireOp",EDGE,"E33.MirrorC"),sQuery(id+"F0.wireOp",EDGE,"E34.MirrorCS"),sQuery(id+"F0.wireOp",EDGE,"E39.MirrorCS"),sQuery(id+"F0.wireOp",EDGE,"E42.MirrorCS"),sQuery(id+"F0.wireOp",EDGE,"E46"),sQuery(id+"F0.wireOp",EDGE,"E48"),subQ0])]})]}),makeQuery(id+"F7.opExtrude","SWEPT_FACE",FACE,{"disambiguationData":[OSD([sQuery(id+"F6.wireOp",EDGE,"E50.0.2")])]})]}),makeQuery(id+"F10.opExtrude","SWEPT_FACE",FACE,{"disambiguationData":[OSD([sQuery(id+"F9.wireOp",EDGE,"E58")])]})]});}
            var Q23;
            Q23=makeQuery(id+"F1.opExtrude","CAP_EDGE",EDGE,{"disambiguationData":[OSD([sQuery(id+"F0.wireOp",EDGE,"E6")])],"isStart":false});
            var Q24;
            Q24=makeQuery(id+"F2.opExtrude","SWEPT_EDGE",EDGE,{"disambiguationData":[OSD([sQuery(id+"F0.wireOp",EDGE,"E32.MirrorCS"),sQuery(id+"F0.wireOp",EDGE,"E42.MirrorCS")])]});
            var Q25;
            Q25=makeQuery(id+"F4.opExtrude","CAP_EDGE",EDGE,{"disambiguationData":[OSD([sQuery(id+"F0.wireOp",EDGE,"E42.MirrorCS")])],"isStart":false});
            var Q26;
            Q26=makeQuery(id+"F10.boolean.opBoolean","INTERSECT",EDGE,{"derivedFrom":[makeQuery(id+"F7.opExtrude","SWEPT_FACE",FACE,{"disambiguationData":[OSD([sQuery(id+"F6.wireOp",EDGE,"E51.0.1"),sQuery(id+"F6.wireOp",EDGE,"E51.0.2"),sQuery(id+"F6.wireOp",EDGE,"E51.0.3")])]}),makeQuery(id+"F10.opExtrude","SWEPT_FACE",FACE,{"disambiguationData":[OSD([sQuery(id+"F9.wireOp",EDGE,"E59")])]})]});
            var Q27;
            {var subQ0=sQuery(id+"F0.wireOp",EDGE,"E42.MirrorCS");var subQ1=makeQuery(id+"F0.imprint","INTERSECT",VERTEX,{"derivedFrom":[sQuery(id+"F0.wireOp",EDGE,"E32.MirrorCS"),subQ0]});Q27=makeQuery(id+"F1.opExtrude","CAP_EDGE",EDGE,{"disambiguationData":[OSD([subQ0]),TDD([makeQuery(id+"F0.imprint","IMPRINT",EDGE,{"disambiguationData":[TD([[subQ1,1.0]])],"derivedFrom":subQ0}),makeQuery(id+"F0.imprint","IMPRINT",EDGE,{"disambiguationData":[TD([[subQ1,-1.0]])],"derivedFrom":subQ0}),makeQuery(id+"F0.imprint","IMPRINT",EDGE,{"disambiguationData":[TD([[makeQuery(id+"F0.imprint","INTERSECT",VERTEX,{"derivedFrom":[sQuery(id+"F0.wireOp",EDGE,"E28.MirrorCS"),subQ0]}),1.0]])],"derivedFrom":subQ0})])],"isStart":false});}
            var Q28;
            {var subQ0=sQuery(id+"F0.wireOp",EDGE,"E42.MirrorCS");var subQ1=makeQuery(id+"F0.imprint","INTERSECT",VERTEX,{"derivedFrom":[subQ0,sQuery(id+"F0.wireOp",EDGE,"E44")]});var subQ2=makeQuery(id+"F0.imprint","INTERSECT",VERTEX,{"derivedFrom":[subQ0,sQuery(id+"F0.wireOp",EDGE,"E45")]});Q28=makeQuery(id+"F1.opExtrude","CAP_EDGE",EDGE,{"disambiguationData":[OSD([subQ0]),TDD([makeQuery(id+"F0.imprint","IMPRINT",EDGE,{"disambiguationData":[TD([[makeQuery(id+"F0.imprint","INTERSECT",VERTEX,{"derivedFrom":[sQuery(id+"F0.wireOp",EDGE,"E25.MirrorCS"),subQ0]}),-1.0]])],"derivedFrom":subQ0}),makeQuery(id+"F0.imprint","IMPRINT",EDGE,{"disambiguationData":[TD([[subQ1,-1.0]])],"derivedFrom":subQ0}),makeQuery(id+"F0.imprint","IMPRINT",EDGE,{"disambiguationData":[TD([[subQ2,-1.0]])],"derivedFrom":subQ0})])],"isStart":false});}
            var Q29;
            Q29=makeQuery(id+"F1.opExtrude","CAP_EDGE",EDGE,{"disambiguationData":[OSD([sQuery(id+"F0.wireOp",EDGE,"E0")])],"isStart":false});
            var Q30;
            Q30=makeQuery(id+"F2.opExtrude","CAP_EDGE",EDGE,{"disambiguationData":[OSD([sQuery(id+"F0.wireOp",EDGE,"E23"),sQuery(id+"F0.wireOp",EDGE,"E35.MirrorCS")])],"isStart":false});
            var Q31;
            Q31=makeQuery(id+"F10.boolean.opBoolean","INTERSECT",EDGE,{"derivedFrom":[makeQuery(id+"F7.opExtrude","SWEPT_FACE",FACE,{"disambiguationData":[OSD([sQuery(id+"F6.wireOp",EDGE,"E51.0.1"),sQuery(id+"F6.wireOp",EDGE,"E51.0.2"),sQuery(id+"F6.wireOp",EDGE,"E51.0.3")])]}),makeQuery(id+"F10.opExtrude","SWEPT_FACE",FACE,{"disambiguationData":[OSD([sQuery(id+"F9.wireOp",EDGE,"E58")])]})]});
            var Q32;
            {var subQ0=sQuery(id+"F0.wireOp",EDGE,"E44");var subQ1=sQuery(id+"F0.wireOp",EDGE,"E47");Q32=makeQuery(id+"F3.boolean.opBoolean","MERGE",EDGE,{"derivedFrom":[makeQuery(id+"F2.opExtrude","SWEPT_EDGE",EDGE,{"disambiguationData":[OSD([subQ0,subQ1])]}),makeQuery(id+"F3.opExtrude","SWEPT_EDGE",EDGE,{"disambiguationData":[OSD([sQuery(id+"F0.wireOp",EDGE,"E0"),sQuery(id+"F0.wireOp",EDGE,"E3"),sQuery(id+"F0.wireOp",EDGE,"E6"),sQuery(id+"F0.wireOp",EDGE,"E7"),sQuery(id+"F0.wireOp",EDGE,"E10.MirrorCS"),sQuery(id+"F0.wireOp",EDGE,"E11.MirrorC"),sQuery(id+"F0.wireOp",EDGE,"E13.MirrorC"),sQuery(id+"F0.wireOp",EDGE,"E19"),sQuery(id+"F0.wireOp",EDGE,"E20"),sQuery(id+"F0.wireOp",EDGE,"E25.MirrorCS"),sQuery(id+"F0.wireOp",EDGE,"E28.MirrorCS"),sQuery(id+"F0.wireOp",EDGE,"E30.MirrorC"),sQuery(id+"F0.wireOp",EDGE,"E33.MirrorC"),sQuery(id+"F0.wireOp",EDGE,"E34.MirrorCS"),sQuery(id+"F0.wireOp",EDGE,"E39.MirrorCS"),sQuery(id+"F0.wireOp",EDGE,"E42.MirrorCS"),subQ0,sQuery(id+"F0.wireOp",EDGE,"E46"),subQ1,sQuery(id+"F0.wireOp",EDGE,"E48")])]})]});}
            var Q33;
            Q33=makeQuery(id+"F4.opExtrude","CAP_EDGE",EDGE,{"disambiguationData":[OSD([sQuery(id+"F0.wireOp",EDGE,"E25.MirrorCS")])],"isStart":false});
            var Q34;
            Q34=makeQuery(id+"F4.opExtrude","SWEPT_EDGE",EDGE,{"disambiguationData":[OSD([sQuery(id+"F0.wireOp",EDGE,"E25.MirrorCS"),sQuery(id+"F0.wireOp",EDGE,"E42.MirrorCS")])]});
            var Q35;
            Q35=makeQuery(id+"F2.opExtrude","SWEPT_EDGE",EDGE,{"disambiguationData":[OSD([sQuery(id+"F0.wireOp",EDGE,"E42.MirrorCS"),sQuery(id+"F0.wireOp",EDGE,"E45")])]});
            var Q36;
            {var subQ0=sQuery(id+"F0.wireOp",EDGE,"E42.MirrorCS");var subQ1=makeQuery(id+"F0.imprint","INTERSECT",VERTEX,{"derivedFrom":[subQ0,sQuery(id+"F0.wireOp",EDGE,"E44")]});Q36=makeQuery(id+"F2.opExtrude","CAP_EDGE",EDGE,{"disambiguationData":[OSD([subQ0]),TDD([makeQuery(id+"F0.imprint","IMPRINT",EDGE,{"disambiguationData":[TD([[makeQuery(id+"F0.imprint","INTERSECT",VERTEX,{"derivedFrom":[sQuery(id+"F0.wireOp",EDGE,"E25.MirrorCS"),subQ0]}),-1.0]])],"derivedFrom":subQ0}),makeQuery(id+"F0.imprint","IMPRINT",EDGE,{"disambiguationData":[TD([[subQ1,-1.0]])],"derivedFrom":subQ0})])],"isStart":false});}
            var Q37;
            {var subQ0=sQuery(id+"F0.wireOp",EDGE,"E47");var subQ1=sQuery(id+"F9.wireOp",EDGE,"E60.trimOffspring");Q37=makeQuery(id+"F10.boolean.opBoolean","INTERSECT",EDGE,{"derivedFrom":[makeQuery(id+"F7.boolean.opBoolean","MERGE",FACE,{"derivedFrom":[makeQuery(id+"F3.boolean.opBoolean","MERGE",FACE,{"derivedFrom":[makeQuery(id+"F2.opExtrude","SWEPT_FACE",FACE,{"disambiguationData":[OSD([subQ0])]}),makeQuery(id+"F3.opExtrude","SWEPT_FACE",FACE,{"disambiguationData":[OSD([sQuery(id+"F0.wireOp",EDGE,"E0"),sQuery(id+"F0.wireOp",EDGE,"E3"),sQuery(id+"F0.wireOp",EDGE,"E6"),sQuery(id+"F0.wireOp",EDGE,"E7"),sQuery(id+"F0.wireOp",EDGE,"E10.MirrorCS"),sQuery(id+"F0.wireOp",EDGE,"E11.MirrorC"),sQuery(id+"F0.wireOp",EDGE,"E13.MirrorC"),sQuery(id+"F0.wireOp",EDGE,"E19"),sQuery(id+"F0.wireOp",EDGE,"E20"),sQuery(id+"F0.wireOp",EDGE,"E25.MirrorCS"),sQuery(id+"F0.wireOp",EDGE,"E28.MirrorCS"),sQuery(id+"F0.wireOp",EDGE,"E30.MirrorC"),sQuery(id+"F0.wireOp",EDGE,"E33.MirrorC"),sQuery(id+"F0.wireOp",EDGE,"E34.MirrorCS"),sQuery(id+"F0.wireOp",EDGE,"E39.MirrorCS"),sQuery(id+"F0.wireOp",EDGE,"E42.MirrorCS"),sQuery(id+"F0.wireOp",EDGE,"E46"),subQ0,sQuery(id+"F0.wireOp",EDGE,"E48")])]})]}),makeQuery(id+"F7.opExtrude","SWEPT_FACE",FACE,{"disambiguationData":[OSD([sQuery(id+"F6.wireOp",EDGE,"E51.0.5")])]})]}),makeQuery(id+"F10.opExtrude","SWEPT_FACE",FACE,{"disambiguationData":[OSD([subQ1]),TDD([makeQuery(id+"F9.imprint","IMPRINT",EDGE,{"disambiguationData":[TD([[makeQuery(id+"F9.imprint","INTERSECT",VERTEX,{"derivedFrom":[sQuery(id+"F9.wireOp",EDGE,"E59"),subQ1]}),-1.0]])],"derivedFrom":subQ1})])]}),makeQuery(id+"F10.opExtrude","SWEPT_FACE",FACE,{"disambiguationData":[OSD([subQ1]),TDD([makeQuery(id+"F9.imprint","IMPRINT",EDGE,{"disambiguationData":[TD([[makeQuery(id+"F9.imprint","INTERSECT",VERTEX,{"derivedFrom":[sQuery(id+"F9.wireOp",EDGE,"E58"),subQ1]}),1.0]])],"derivedFrom":subQ1})])]})]});}
            var Q38;
            {var subQ0=sQuery(id+"F6.wireOp",EDGE,"E51.0.1");var subQ1=sQuery(id+"F6.wireOp",EDGE,"E51.0.2");var subQ2=sQuery(id+"F6.wireOp",EDGE,"E51.0.3");var subQ3=sQuery(id+"F0.wireOp",EDGE,"E20");Q38=makeQuery(id+"F7.boolean.opBoolean","SPLIT",EDGE,{"disambiguationData":[TD([makeQuery(id+"F4.opExtrude","SWEPT_FACE",FACE,{"disambiguationData":[OSD([subQ3])]})])],"derivedFrom":makeQuery(id+"F7.opExtrude","CAP_EDGE",EDGE,{"disambiguationData":[OSD([subQ0,subQ1,subQ2])],"isStart":true})});}
            var Q39;
            Q39=makeQuery(id+"F4.opExtrude","CAP_EDGE",EDGE,{"disambiguationData":[OSD([sQuery(id+"F0.wireOp",EDGE,"E46")])],"isStart":false});
            var Q40;
            Q40=makeQuery(id+"F4.opExtrude","CAP_EDGE",EDGE,{"disambiguationData":[OSD([sQuery(id+"F0.wireOp",EDGE,"E48")])],"isStart":false});
            var Q41;
            Q41=makeQuery(id+"F4.opExtrude","SWEPT_EDGE",EDGE,{"disambiguationData":[OSD([sQuery(id+"F0.wireOp",EDGE,"E19"),sQuery(id+"F0.wireOp",EDGE,"E46")])]});
            var Q42;
            Q42=makeQuery(id+"F4.opExtrude","SWEPT_EDGE",EDGE,{"disambiguationData":[OSD([sQuery(id+"F0.wireOp",EDGE,"E20"),sQuery(id+"F0.wireOp",EDGE,"E46")])]});
            var Q43;
            Q43=makeQuery(id+"F4.opExtrude","SWEPT_EDGE",EDGE,{"disambiguationData":[OSD([sQuery(id+"F0.wireOp",EDGE,"E25.MirrorCS"),sQuery(id+"F0.wireOp",EDGE,"E48")])]});
            var Q44;
            {var subQ0=sQuery(id+"F6.wireOp",EDGE,"E51.0.1");var subQ1=sQuery(id+"F6.wireOp",EDGE,"E51.0.2");var subQ2=sQuery(id+"F6.wireOp",EDGE,"E51.0.3");var subQ3=sQuery(id+"F0.wireOp",EDGE,"E19");Q44=makeQuery(id+"F7.boolean.opBoolean","SPLIT",EDGE,{"disambiguationData":[TD([makeQuery(id+"F4.opExtrude","SWEPT_FACE",FACE,{"disambiguationData":[OSD([subQ3])]})])],"derivedFrom":makeQuery(id+"F7.opExtrude","CAP_EDGE",EDGE,{"disambiguationData":[OSD([subQ0,subQ1,subQ2])],"isStart":true})});}
            var Q45;
            {var subQ0=sQuery(id+"F0.wireOp",EDGE,"E47");Q45=makeQuery(id+"F10.boolean.opBoolean","INTERSECT",EDGE,{"derivedFrom":[makeQuery(id+"F7.boolean.opBoolean","MERGE",FACE,{"derivedFrom":[makeQuery(id+"F3.boolean.opBoolean","MERGE",FACE,{"derivedFrom":[makeQuery(id+"F2.opExtrude","SWEPT_FACE",FACE,{"disambiguationData":[OSD([subQ0])]}),makeQuery(id+"F3.opExtrude","SWEPT_FACE",FACE,{"disambiguationData":[OSD([sQuery(id+"F0.wireOp",EDGE,"E0"),sQuery(id+"F0.wireOp",EDGE,"E3"),sQuery(id+"F0.wireOp",EDGE,"E6"),sQuery(id+"F0.wireOp",EDGE,"E7"),sQuery(id+"F0.wireOp",EDGE,"E10.MirrorCS"),sQuery(id+"F0.wireOp",EDGE,"E11.MirrorC"),sQuery(id+"F0.wireOp",EDGE,"E13.MirrorC"),sQuery(id+"F0.wireOp",EDGE,"E19"),sQuery(id+"F0.wireOp",EDGE,"E20"),sQuery(id+"F0.wireOp",EDGE,"E25.MirrorCS"),sQuery(id+"F0.wireOp",EDGE,"E28.MirrorCS"),sQuery(id+"F0.wireOp",EDGE,"E30.MirrorC"),sQuery(id+"F0.wireOp",EDGE,"E33.MirrorC"),sQuery(id+"F0.wireOp",EDGE,"E34.MirrorCS"),sQuery(id+"F0.wireOp",EDGE,"E39.MirrorCS"),sQuery(id+"F0.wireOp",EDGE,"E42.MirrorCS"),sQuery(id+"F0.wireOp",EDGE,"E46"),subQ0,sQuery(id+"F0.wireOp",EDGE,"E48")])]})]}),makeQuery(id+"F7.opExtrude","SWEPT_FACE",FACE,{"disambiguationData":[OSD([sQuery(id+"F6.wireOp",EDGE,"E51.0.5")])]})]}),makeQuery(id+"F10.opExtrude","SWEPT_FACE",FACE,{"disambiguationData":[OSD([sQuery(id+"F9.wireOp",EDGE,"E58")])]})]});}
            var Q46;
            Q46=makeQuery(id+"F10.boolean.opBoolean","MERGE",EDGE,{"derivedFrom":[makeQuery(id+"F7.opExtrude","CAP_EDGE",EDGE,{"disambiguationData":[OSD([sQuery(id+"F6.wireOp",EDGE,"E51.0.0")])],"isStart":true}),makeQuery(id+"F10.opExtrude","SWEPT_EDGE",EDGE,{"disambiguationData":[OSD([sQuery(id+"F9.wireOp",EDGE,"E54.0.4"),sQuery(id+"F9.wireOp",EDGE,"E59"),sQuery(id+"F9.wireOp",EDGE,"E54.0.5")])]})]});
            var Q47;
            Q47=makeQuery(id+"F10.boolean.opBoolean","MERGE",EDGE,{"derivedFrom":[makeQuery(id+"F7.opExtrude","CAP_EDGE",EDGE,{"disambiguationData":[OSD([sQuery(id+"F6.wireOp",EDGE,"E51.0.4")])],"isStart":true}),makeQuery(id+"F10.opExtrude","SWEPT_EDGE",EDGE,{"disambiguationData":[OSD([sQuery(id+"F9.wireOp",EDGE,"E54.0.0"),sQuery(id+"F9.wireOp",EDGE,"E58"),sQuery(id+"F9.wireOp",EDGE,"E61")])]})]});
            var Q48;
            {var subQ0=sQuery(id+"F0.wireOp",EDGE,"E3");var subQ1=makeQuery(id+"F0.imprint","INTERSECT",VERTEX,{"derivedFrom":[subQ0,sQuery(id+"F0.wireOp",EDGE,"E44")]});Q48=makeQuery(id+"F2.opExtrude","CAP_EDGE",EDGE,{"disambiguationData":[OSD([subQ0]),TDD([makeQuery(id+"F0.imprint","IMPRINT",EDGE,{"disambiguationData":[TD([[makeQuery(id+"F0.imprint","INTERSECT",VERTEX,{"derivedFrom":[subQ0,sQuery(id+"F0.wireOp",EDGE,"E20")]}),-1.0]])],"derivedFrom":subQ0}),makeQuery(id+"F0.imprint","IMPRINT",EDGE,{"disambiguationData":[TD([[subQ1,-1.0]])],"derivedFrom":subQ0})])],"isStart":false});}
            var Q49;
            Q49=makeQuery(id+"F2.opExtrude","SWEPT_EDGE",EDGE,{"disambiguationData":[OSD([sQuery(id+"F0.wireOp",EDGE,"E3"),sQuery(id+"F0.wireOp",EDGE,"E24")])]});
            var Q50;
            Q50=makeQuery(id+"F10.boolean.opBoolean","COPY",EDGE,{"disambiguationData":[OD(1.0)],"derivedFrom":makeQuery(id+"F10.opExtrude","SWEPT_EDGE",EDGE,{"disambiguationData":[OSD([sQuery(id+"F9.wireOp",EDGE,"E58"),sQuery(id+"F9.wireOp",EDGE,"E60.trimOffspring")])]})});
            var Q51;
            {var subQ0=sQuery(id+"F0.wireOp",EDGE,"E42.MirrorCS");Q51=makeQuery(id+"F2.opExtrude","CAP_EDGE",EDGE,{"disambiguationData":[OSD([subQ0]),TDD([makeQuery(id+"F0.imprint","IMPRINT",EDGE,{"disambiguationData":[TD([[makeQuery(id+"F0.imprint","INTERSECT",VERTEX,{"derivedFrom":[sQuery(id+"F0.wireOp",EDGE,"E32.MirrorCS"),subQ0]}),-1.0]])],"derivedFrom":subQ0}),makeQuery(id+"F0.imprint","IMPRINT",EDGE,{"disambiguationData":[TD([[makeQuery(id+"F0.imprint","INTERSECT",VERTEX,{"derivedFrom":[sQuery(id+"F0.wireOp",EDGE,"E28.MirrorCS"),subQ0]}),1.0]])],"derivedFrom":subQ0})])],"isStart":false});}
            var Q52;
            Q52=makeQuery(id+"F2.boolean.opBoolean","INTERSECT",EDGE,{"derivedFrom":[makeQuery(id+"F1.opExtrude","CAP_FACE",FACE,{"disambiguationData":[OSD([sQuery(id+"F0.wireOp",EDGE,"E0"),sQuery(id+"F0.wireOp",EDGE,"E3"),sQuery(id+"F0.wireOp",EDGE,"E6"),sQuery(id+"F0.wireOp",EDGE,"E7"),sQuery(id+"F0.wireOp",EDGE,"E10.MirrorCS"),sQuery(id+"F0.wireOp",EDGE,"E11.MirrorC"),sQuery(id+"F0.wireOp",EDGE,"E13.MirrorC"),sQuery(id+"F0.wireOp",EDGE,"E19"),sQuery(id+"F0.wireOp",EDGE,"E20"),sQuery(id+"F0.wireOp",EDGE,"E25.MirrorCS"),sQuery(id+"F0.wireOp",EDGE,"E28.MirrorCS"),sQuery(id+"F0.wireOp",EDGE,"E30.MirrorC"),sQuery(id+"F0.wireOp",EDGE,"E33.MirrorC"),sQuery(id+"F0.wireOp",EDGE,"E34.MirrorCS"),sQuery(id+"F0.wireOp",EDGE,"E39.MirrorCS"),sQuery(id+"F0.wireOp",EDGE,"E42.MirrorCS"),sQuery(id+"F0.wireOp",EDGE,"E46"),sQuery(id+"F0.wireOp",EDGE,"E48")])],"isStart":false}),makeQuery(id+"F2.opExtrude","SWEPT_FACE",FACE,{"disambiguationData":[OSD([sQuery(id+"F0.wireOp",EDGE,"E24"),sQuery(id+"F0.wireOp",EDGE,"E32.MirrorCS")])]})]});
            var Q53;
            Q53=makeQuery(id+"F2.opExtrude","SWEPT_EDGE",EDGE,{"disambiguationData":[OSD([sQuery(id+"F0.wireOp",EDGE,"E3"),sQuery(id+"F0.wireOp",EDGE,"E45")])]});
            var Q54;
            Q54=makeQuery(id+"F10.boolean.opBoolean","COPY",EDGE,{"disambiguationData":[OD(0.0)],"derivedFrom":makeQuery(id+"F10.opExtrude","SWEPT_EDGE",EDGE,{"disambiguationData":[OSD([sQuery(id+"F9.wireOp",EDGE,"E59"),sQuery(id+"F9.wireOp",EDGE,"E60.trimOffspring")])]})});
            var Q55;
            {var subQ0=sQuery(id+"F0.wireOp",EDGE,"E3");var subQ2=makeQuery(id+"F0.imprint","INTERSECT",VERTEX,{"derivedFrom":[subQ0,sQuery(id+"F0.wireOp",EDGE,"E23")]});Q55=makeQuery(id+"F1.opExtrude","CAP_EDGE",EDGE,{"disambiguationData":[OSD([subQ0]),TDD([makeQuery(id+"F0.imprint","IMPRINT",EDGE,{"disambiguationData":[TD([[makeQuery(id+"F0.imprint","INTERSECT",VERTEX,{"derivedFrom":[sQuery(id+"F0.wireOp",EDGE,"E0"),subQ0]}),-1.0]])],"derivedFrom":subQ0}),makeQuery(id+"F0.imprint","IMPRINT",EDGE,{"disambiguationData":[TD([[subQ2,1.0]])],"derivedFrom":subQ0}),makeQuery(id+"F0.imprint","IMPRINT",EDGE,{"disambiguationData":[TD([[makeQuery(id+"F0.imprint","INTERSECT",VERTEX,{"derivedFrom":[subQ0,sQuery(id+"F0.wireOp",EDGE,"E19")]}),1.0]])],"derivedFrom":subQ0})])],"isStart":false});}
            var Q56;
            {var subQ0=sQuery(id+"F0.wireOp",EDGE,"E3");var subQ1=makeQuery(id+"F0.imprint","INTERSECT",VERTEX,{"derivedFrom":[subQ0,sQuery(id+"F0.wireOp",EDGE,"E44")]});Q56=makeQuery(id+"F1.opExtrude","CAP_EDGE",EDGE,{"disambiguationData":[OSD([subQ0]),TDD([makeQuery(id+"F0.imprint","IMPRINT",EDGE,{"disambiguationData":[TD([[makeQuery(id+"F0.imprint","INTERSECT",VERTEX,{"derivedFrom":[subQ0,sQuery(id+"F0.wireOp",EDGE,"E20")]}),-1.0]])],"derivedFrom":subQ0}),makeQuery(id+"F0.imprint","IMPRINT",EDGE,{"disambiguationData":[TD([[subQ1,-1.0]])],"derivedFrom":subQ0}),makeQuery(id+"F0.imprint","IMPRINT",EDGE,{"disambiguationData":[TD([[makeQuery(id+"F0.imprint","INTERSECT",VERTEX,{"derivedFrom":[subQ0,sQuery(id+"F0.wireOp",EDGE,"E11.MirrorC")]}),1.0]])],"derivedFrom":subQ0})])],"isStart":false});}
            var Q57;
            {var subQ0=sQuery(id+"F0.wireOp",EDGE,"E23");var subQ1=sQuery(id+"F0.wireOp",EDGE,"E47");Q57=makeQuery(id+"F3.boolean.opBoolean","MERGE",EDGE,{"derivedFrom":[makeQuery(id+"F2.opExtrude","SWEPT_EDGE",EDGE,{"disambiguationData":[OSD([subQ0,subQ1])]}),makeQuery(id+"F3.opExtrude","SWEPT_EDGE",EDGE,{"disambiguationData":[OSD([sQuery(id+"F0.wireOp",EDGE,"E0"),sQuery(id+"F0.wireOp",EDGE,"E3"),sQuery(id+"F0.wireOp",EDGE,"E6"),sQuery(id+"F0.wireOp",EDGE,"E7"),sQuery(id+"F0.wireOp",EDGE,"E10.MirrorCS"),sQuery(id+"F0.wireOp",EDGE,"E11.MirrorC"),sQuery(id+"F0.wireOp",EDGE,"E13.MirrorC"),sQuery(id+"F0.wireOp",EDGE,"E19"),sQuery(id+"F0.wireOp",EDGE,"E20"),subQ0,sQuery(id+"F0.wireOp",EDGE,"E25.MirrorCS"),sQuery(id+"F0.wireOp",EDGE,"E28.MirrorCS"),sQuery(id+"F0.wireOp",EDGE,"E30.MirrorC"),sQuery(id+"F0.wireOp",EDGE,"E33.MirrorC"),sQuery(id+"F0.wireOp",EDGE,"E34.MirrorCS"),sQuery(id+"F0.wireOp",EDGE,"E35.MirrorCS"),sQuery(id+"F0.wireOp",EDGE,"E39.MirrorCS"),sQuery(id+"F0.wireOp",EDGE,"E42.MirrorCS"),sQuery(id+"F0.wireOp",EDGE,"E46"),subQ1,sQuery(id+"F0.wireOp",EDGE,"E48")])]})]});}
            var Q58;
            {var subQ0=sQuery(id+"F0.wireOp",EDGE,"E35.MirrorCS");var subQ1=sQuery(id+"F0.wireOp",EDGE,"E49");Q58=makeQuery(id+"F3.boolean.opBoolean","MERGE",EDGE,{"derivedFrom":[makeQuery(id+"F2.opExtrude","SWEPT_EDGE",EDGE,{"disambiguationData":[OSD([subQ0,subQ1])]}),makeQuery(id+"F3.opExtrude","SWEPT_EDGE",EDGE,{"disambiguationData":[OSD([sQuery(id+"F0.wireOp",EDGE,"E0"),sQuery(id+"F0.wireOp",EDGE,"E3"),sQuery(id+"F0.wireOp",EDGE,"E6"),sQuery(id+"F0.wireOp",EDGE,"E7"),sQuery(id+"F0.wireOp",EDGE,"E10.MirrorCS"),sQuery(id+"F0.wireOp",EDGE,"E11.MirrorC"),sQuery(id+"F0.wireOp",EDGE,"E13.MirrorC"),sQuery(id+"F0.wireOp",EDGE,"E19"),sQuery(id+"F0.wireOp",EDGE,"E20"),sQuery(id+"F0.wireOp",EDGE,"E23"),sQuery(id+"F0.wireOp",EDGE,"E25.MirrorCS"),sQuery(id+"F0.wireOp",EDGE,"E28.MirrorCS"),sQuery(id+"F0.wireOp",EDGE,"E30.MirrorC"),sQuery(id+"F0.wireOp",EDGE,"E33.MirrorC"),sQuery(id+"F0.wireOp",EDGE,"E34.MirrorCS"),subQ0,sQuery(id+"F0.wireOp",EDGE,"E39.MirrorCS"),sQuery(id+"F0.wireOp",EDGE,"E42.MirrorCS"),sQuery(id+"F0.wireOp",EDGE,"E46"),sQuery(id+"F0.wireOp",EDGE,"E48"),subQ1])]})]});}
            var Q59;
            {var subQ0=sQuery(id+"F0.wireOp",EDGE,"E44");var subQ1=sQuery(id+"F0.wireOp",EDGE,"E49");Q59=makeQuery(id+"F3.boolean.opBoolean","MERGE",EDGE,{"derivedFrom":[makeQuery(id+"F2.opExtrude","SWEPT_EDGE",EDGE,{"disambiguationData":[OSD([subQ0,subQ1])]}),makeQuery(id+"F3.opExtrude","SWEPT_EDGE",EDGE,{"disambiguationData":[OSD([sQuery(id+"F0.wireOp",EDGE,"E0"),sQuery(id+"F0.wireOp",EDGE,"E3"),sQuery(id+"F0.wireOp",EDGE,"E6"),sQuery(id+"F0.wireOp",EDGE,"E7"),sQuery(id+"F0.wireOp",EDGE,"E10.MirrorCS"),sQuery(id+"F0.wireOp",EDGE,"E11.MirrorC"),sQuery(id+"F0.wireOp",EDGE,"E13.MirrorC"),sQuery(id+"F0.wireOp",EDGE,"E19"),sQuery(id+"F0.wireOp",EDGE,"E20"),sQuery(id+"F0.wireOp",EDGE,"E25.MirrorCS"),sQuery(id+"F0.wireOp",EDGE,"E28.MirrorCS"),sQuery(id+"F0.wireOp",EDGE,"E30.MirrorC"),sQuery(id+"F0.wireOp",EDGE,"E33.MirrorC"),sQuery(id+"F0.wireOp",EDGE,"E34.MirrorCS"),sQuery(id+"F0.wireOp",EDGE,"E39.MirrorCS"),sQuery(id+"F0.wireOp",EDGE,"E42.MirrorCS"),subQ0,sQuery(id+"F0.wireOp",EDGE,"E46"),sQuery(id+"F0.wireOp",EDGE,"E48"),subQ1])]})]});}
            var Q60;
            Q60=makeQuery(id+"F4.opExtrude","CAP_EDGE",EDGE,{"disambiguationData":[OSD([sQuery(id+"F0.wireOp",EDGE,"E20")])],"isStart":false});
            var Q61;
            Q61=makeQuery(id+"F4.opExtrude","SWEPT_EDGE",EDGE,{"disambiguationData":[OSD([sQuery(id+"F0.wireOp",EDGE,"E28.MirrorCS"),sQuery(id+"F0.wireOp",EDGE,"E42.MirrorCS")])]});
            var Q62;
            Q62=makeQuery(id+"F4.opExtrude","CAP_EDGE",EDGE,{"disambiguationData":[OSD([sQuery(id+"F0.wireOp",EDGE,"E3")])],"isStart":false});
            var Q63;
            Q63=makeQuery(id+"F2.opExtrude","CAP_EDGE",EDGE,{"disambiguationData":[OSD([sQuery(id+"F0.wireOp",EDGE,"E20")])],"isStart":false});
            var Q64;
            Q64=makeQuery(id+"F2.opExtrude","CAP_EDGE",EDGE,{"disambiguationData":[OSD([sQuery(id+"F0.wireOp",EDGE,"E25.MirrorCS")])],"isStart":false});
            var Q65;
            Q65=makeQuery(id+"F2.opExtrude","CAP_EDGE",EDGE,{"disambiguationData":[OSD([sQuery(id+"F0.wireOp",EDGE,"E28.MirrorCS")])],"isStart":false});
            var Q66;
            Q66=makeQuery(id+"F10.boolean.opBoolean","COPY",EDGE,{"disambiguationData":[OD(1.0)],"derivedFrom":makeQuery(id+"F10.opExtrude","SWEPT_EDGE",EDGE,{"disambiguationData":[OSD([sQuery(id+"F9.wireOp",EDGE,"E59"),sQuery(id+"F9.wireOp",EDGE,"E60.trimOffspring")])]})});
            var Q67;
            Q67=makeQuery(id+"F4.opExtrude","SWEPT_EDGE",EDGE,{"disambiguationData":[OSD([sQuery(id+"F0.wireOp",EDGE,"E3"),sQuery(id+"F0.wireOp",EDGE,"E19")])]});
            var Q68;
            Q68=makeQuery(id+"F2.boolean.opBoolean","INTERSECT",EDGE,{"derivedFrom":[makeQuery(id+"F1.opExtrude","CAP_FACE",FACE,{"disambiguationData":[OSD([sQuery(id+"F0.wireOp",EDGE,"E0"),sQuery(id+"F0.wireOp",EDGE,"E3"),sQuery(id+"F0.wireOp",EDGE,"E6"),sQuery(id+"F0.wireOp",EDGE,"E7"),sQuery(id+"F0.wireOp",EDGE,"E10.MirrorCS"),sQuery(id+"F0.wireOp",EDGE,"E11.MirrorC"),sQuery(id+"F0.wireOp",EDGE,"E13.MirrorC"),sQuery(id+"F0.wireOp",EDGE,"E19"),sQuery(id+"F0.wireOp",EDGE,"E20"),sQuery(id+"F0.wireOp",EDGE,"E25.MirrorCS"),sQuery(id+"F0.wireOp",EDGE,"E28.MirrorCS"),sQuery(id+"F0.wireOp",EDGE,"E30.MirrorC"),sQuery(id+"F0.wireOp",EDGE,"E33.MirrorC"),sQuery(id+"F0.wireOp",EDGE,"E34.MirrorCS"),sQuery(id+"F0.wireOp",EDGE,"E39.MirrorCS"),sQuery(id+"F0.wireOp",EDGE,"E42.MirrorCS"),sQuery(id+"F0.wireOp",EDGE,"E46"),sQuery(id+"F0.wireOp",EDGE,"E48")])],"isStart":false}),makeQuery(id+"F2.opExtrude","SWEPT_FACE",FACE,{"disambiguationData":[OSD([sQuery(id+"F0.wireOp",EDGE,"E45")])]})]});
            var Q69;
            Q69=makeQuery(id+"F2.opExtrude","CAP_EDGE",EDGE,{"disambiguationData":[OSD([sQuery(id+"F0.wireOp",EDGE,"E19")])],"isStart":false});
            var Q70;
            Q70=makeQuery(id+"F4.opExtrude","CAP_EDGE",EDGE,{"disambiguationData":[OSD([sQuery(id+"F0.wireOp",EDGE,"E19")])],"isStart":false});
            var Q71;
            Q71=makeQuery(id+"F4.opExtrude","SWEPT_EDGE",EDGE,{"disambiguationData":[OSD([sQuery(id+"F0.wireOp",EDGE,"E3"),sQuery(id+"F0.wireOp",EDGE,"E20")])]});
            fillet(context, id + "F11", {"entities" : qUnion([Q0, Q1, Q2, Q3, Q4, Q5, Q6, Q7, Q8, Q9, Q10, Q11, Q12, Q13, Q14, Q15, Q16, Q17, Q18, Q19, Q20, Q21, Q22, Q23, Q24, Q25, Q26, Q27, Q28, Q29, Q30, Q31, Q32, Q33, Q34, Q35, Q36, Q37, Q38, Q39, Q40, Q41, Q42, Q43, Q44, Q45, Q46, Q47, Q48, Q49, Q50, Q51, Q52, Q53, Q54, Q55, Q56, Q57, Q58, Q59, Q60, Q61, Q62, Q63, Q64, Q65, Q66, Q67, Q68, Q69, Q70, Q71]), "radius" : 1.59 * mm, "tangentPropagation" : true, "allowEdgeOverflow" : false});
        }
        {
            var Q0;
            Q0=makeQuery(id+"F4.opExtrude","SWEPT_EDGE",EDGE,{"disambiguationData":[OSD([sQuery(id+"F0.wireOp",EDGE,"E25.MirrorCS"),sQuery(id+"F0.wireOp",EDGE,"E48")])]});
            var Q1;
            Q1=makeQuery(id+"F4.opExtrude","SWEPT_EDGE",EDGE,{"disambiguationData":[OSD([sQuery(id+"F0.wireOp",EDGE,"E28.MirrorCS"),sQuery(id+"F0.wireOp",EDGE,"E48")])]});
            var Q2;
            Q2=makeQuery(id+"F4.opExtrude","SWEPT_EDGE",EDGE,{"disambiguationData":[OSD([sQuery(id+"F0.wireOp",EDGE,"E19"),sQuery(id+"F0.wireOp",EDGE,"E46")])]});
            var Q3;
            Q3=makeQuery(id+"F4.opExtrude","SWEPT_EDGE",EDGE,{"disambiguationData":[OSD([sQuery(id+"F0.wireOp",EDGE,"E20"),sQuery(id+"F0.wireOp",EDGE,"E46")])]});
            var Q4;
            Q4=makeQuery(id+"F2.opExtrude","CAP_EDGE",EDGE,{"disambiguationData":[OSD([sQuery(id+"F0.wireOp",EDGE,"E45")])],"isStart":false});
            var Q5;
            Q5=makeQuery(id+"F2.opExtrude","CAP_EDGE",EDGE,{"disambiguationData":[OSD([sQuery(id+"F0.wireOp",EDGE,"E24"),sQuery(id+"F0.wireOp",EDGE,"E32.MirrorCS")])],"isStart":false});
            var Q6;
            Q6=makeQuery(id+"F2.boolean.opBoolean","INTERSECT",EDGE,{"derivedFrom":[makeQuery(id+"F1.opExtrude","CAP_FACE",FACE,{"disambiguationData":[OSD([sQuery(id+"F0.wireOp",EDGE,"E0"),sQuery(id+"F0.wireOp",EDGE,"E3"),sQuery(id+"F0.wireOp",EDGE,"E6"),sQuery(id+"F0.wireOp",EDGE,"E7"),sQuery(id+"F0.wireOp",EDGE,"E10.MirrorCS"),sQuery(id+"F0.wireOp",EDGE,"E11.MirrorC"),sQuery(id+"F0.wireOp",EDGE,"E13.MirrorC"),sQuery(id+"F0.wireOp",EDGE,"E19"),sQuery(id+"F0.wireOp",EDGE,"E20"),sQuery(id+"F0.wireOp",EDGE,"E25.MirrorCS"),sQuery(id+"F0.wireOp",EDGE,"E28.MirrorCS"),sQuery(id+"F0.wireOp",EDGE,"E30.MirrorC"),sQuery(id+"F0.wireOp",EDGE,"E33.MirrorC"),sQuery(id+"F0.wireOp",EDGE,"E34.MirrorCS"),sQuery(id+"F0.wireOp",EDGE,"E39.MirrorCS"),sQuery(id+"F0.wireOp",EDGE,"E42.MirrorCS"),sQuery(id+"F0.wireOp",EDGE,"E46"),sQuery(id+"F0.wireOp",EDGE,"E48")])],"isStart":false}),makeQuery(id+"F2.opExtrude","SWEPT_FACE",FACE,{"disambiguationData":[OSD([sQuery(id+"F0.wireOp",EDGE,"E24"),sQuery(id+"F0.wireOp",EDGE,"E32.MirrorCS")])]})]});
            var Q7;
            Q7=makeQuery(id+"F1.opExtrude","CAP_EDGE",EDGE,{"disambiguationData":[OSD([sQuery(id+"F0.wireOp",EDGE,"E6")])],"isStart":false});
            var Q8;
            Q8=makeQuery(id+"F1.opExtrude","CAP_EDGE",EDGE,{"disambiguationData":[OSD([sQuery(id+"F0.wireOp",EDGE,"E39.MirrorCS")])],"isStart":false});
            var Q9;
            Q9=makeQuery(id+"F1.opExtrude","CAP_EDGE",EDGE,{"disambiguationData":[OSD([sQuery(id+"F0.wireOp",EDGE,"E0")])],"isStart":false});
            var Q10;
            {var subQ0=sQuery(id+"F0.wireOp",EDGE,"E42.MirrorCS");Q10=makeQuery(id+"F2.opExtrude","CAP_EDGE",EDGE,{"disambiguationData":[OSD([subQ0]),TDD([makeQuery(id+"F0.imprint","IMPRINT",EDGE,{"disambiguationData":[TD([[makeQuery(id+"F0.imprint","INTERSECT",VERTEX,{"derivedFrom":[sQuery(id+"F0.wireOp",EDGE,"E32.MirrorCS"),subQ0]}),-1.0]])],"derivedFrom":subQ0}),makeQuery(id+"F0.imprint","IMPRINT",EDGE,{"disambiguationData":[TD([[makeQuery(id+"F0.imprint","INTERSECT",VERTEX,{"derivedFrom":[sQuery(id+"F0.wireOp",EDGE,"E28.MirrorCS"),subQ0]}),1.0]])],"derivedFrom":subQ0})])],"isStart":false});}
            var Q11;
            Q11=makeQuery(id+"F4.opExtrude","SWEPT_EDGE",EDGE,{"disambiguationData":[OSD([sQuery(id+"F0.wireOp",EDGE,"E28.MirrorCS"),sQuery(id+"F0.wireOp",EDGE,"E42.MirrorCS")])]});
            var Q12;
            Q12=makeQuery(id+"F4.opExtrude","SWEPT_EDGE",EDGE,{"disambiguationData":[OSD([sQuery(id+"F0.wireOp",EDGE,"E25.MirrorCS"),sQuery(id+"F0.wireOp",EDGE,"E42.MirrorCS")])]});
            var Q13;
            {var subQ0=sQuery(id+"F0.wireOp",EDGE,"E42.MirrorCS");var subQ1=makeQuery(id+"F0.imprint","INTERSECT",VERTEX,{"derivedFrom":[subQ0,sQuery(id+"F0.wireOp",EDGE,"E44")]});Q13=makeQuery(id+"F2.opExtrude","CAP_EDGE",EDGE,{"disambiguationData":[OSD([subQ0]),TDD([makeQuery(id+"F0.imprint","IMPRINT",EDGE,{"disambiguationData":[TD([[makeQuery(id+"F0.imprint","INTERSECT",VERTEX,{"derivedFrom":[sQuery(id+"F0.wireOp",EDGE,"E25.MirrorCS"),subQ0]}),-1.0]])],"derivedFrom":subQ0}),makeQuery(id+"F0.imprint","IMPRINT",EDGE,{"disambiguationData":[TD([[subQ1,-1.0]])],"derivedFrom":subQ0})])],"isStart":false});}
            var Q14;
            Q14=makeQuery(id+"F2.opExtrude","SWEPT_EDGE",EDGE,{"disambiguationData":[OSD([sQuery(id+"F0.wireOp",EDGE,"E42.MirrorCS"),sQuery(id+"F0.wireOp",EDGE,"E45")])]});
            var Q15;
            Q15=makeQuery(id+"F2.boolean.opBoolean","INTERSECT",EDGE,{"derivedFrom":[makeQuery(id+"F1.opExtrude","CAP_FACE",FACE,{"disambiguationData":[OSD([sQuery(id+"F0.wireOp",EDGE,"E0"),sQuery(id+"F0.wireOp",EDGE,"E3"),sQuery(id+"F0.wireOp",EDGE,"E6"),sQuery(id+"F0.wireOp",EDGE,"E7"),sQuery(id+"F0.wireOp",EDGE,"E10.MirrorCS"),sQuery(id+"F0.wireOp",EDGE,"E11.MirrorC"),sQuery(id+"F0.wireOp",EDGE,"E13.MirrorC"),sQuery(id+"F0.wireOp",EDGE,"E19"),sQuery(id+"F0.wireOp",EDGE,"E20"),sQuery(id+"F0.wireOp",EDGE,"E25.MirrorCS"),sQuery(id+"F0.wireOp",EDGE,"E28.MirrorCS"),sQuery(id+"F0.wireOp",EDGE,"E30.MirrorC"),sQuery(id+"F0.wireOp",EDGE,"E33.MirrorC"),sQuery(id+"F0.wireOp",EDGE,"E34.MirrorCS"),sQuery(id+"F0.wireOp",EDGE,"E39.MirrorCS"),sQuery(id+"F0.wireOp",EDGE,"E42.MirrorCS"),sQuery(id+"F0.wireOp",EDGE,"E46"),sQuery(id+"F0.wireOp",EDGE,"E48")])],"isStart":false}),makeQuery(id+"F2.opExtrude","SWEPT_FACE",FACE,{"disambiguationData":[OSD([sQuery(id+"F0.wireOp",EDGE,"E45")])]})]});
            var Q16;
            {var subQ0=sQuery(id+"F0.wireOp",EDGE,"E42.MirrorCS");var subQ1=makeQuery(id+"F0.imprint","INTERSECT",VERTEX,{"derivedFrom":[subQ0,sQuery(id+"F0.wireOp",EDGE,"E44")]});var subQ2=makeQuery(id+"F0.imprint","INTERSECT",VERTEX,{"derivedFrom":[subQ0,sQuery(id+"F0.wireOp",EDGE,"E45")]});Q16=makeQuery(id+"F1.opExtrude","CAP_EDGE",EDGE,{"disambiguationData":[OSD([subQ0]),TDD([makeQuery(id+"F0.imprint","IMPRINT",EDGE,{"disambiguationData":[TD([[makeQuery(id+"F0.imprint","INTERSECT",VERTEX,{"derivedFrom":[sQuery(id+"F0.wireOp",EDGE,"E25.MirrorCS"),subQ0]}),-1.0]])],"derivedFrom":subQ0}),makeQuery(id+"F0.imprint","IMPRINT",EDGE,{"disambiguationData":[TD([[subQ1,-1.0]])],"derivedFrom":subQ0}),makeQuery(id+"F0.imprint","IMPRINT",EDGE,{"disambiguationData":[TD([[subQ2,-1.0]])],"derivedFrom":subQ0})])],"isStart":false});}
            var Q17;
            Q17=makeQuery(id+"F1.opExtrude","CAP_EDGE",EDGE,{"disambiguationData":[OSD([sQuery(id+"F0.wireOp",EDGE,"E34.MirrorCS")])],"isStart":false});
            var Q18;
            Q18=makeQuery(id+"F1.opExtrude","CAP_EDGE",EDGE,{"disambiguationData":[OSD([sQuery(id+"F0.wireOp",EDGE,"E10.MirrorCS")])],"isStart":false});
            var Q19;
            Q19=makeQuery(id+"F1.opExtrude","CAP_EDGE",EDGE,{"disambiguationData":[OSD([sQuery(id+"F0.wireOp",EDGE,"E11.MirrorC")])],"isStart":false});
            var Q20;
            {var subQ0=sQuery(id+"F0.wireOp",EDGE,"E3");var subQ1=makeQuery(id+"F0.imprint","INTERSECT",VERTEX,{"derivedFrom":[subQ0,sQuery(id+"F0.wireOp",EDGE,"E44")]});Q20=makeQuery(id+"F1.opExtrude","CAP_EDGE",EDGE,{"disambiguationData":[OSD([subQ0]),TDD([makeQuery(id+"F0.imprint","IMPRINT",EDGE,{"disambiguationData":[TD([[makeQuery(id+"F0.imprint","INTERSECT",VERTEX,{"derivedFrom":[subQ0,sQuery(id+"F0.wireOp",EDGE,"E20")]}),-1.0]])],"derivedFrom":subQ0}),makeQuery(id+"F0.imprint","IMPRINT",EDGE,{"disambiguationData":[TD([[subQ1,-1.0]])],"derivedFrom":subQ0}),makeQuery(id+"F0.imprint","IMPRINT",EDGE,{"disambiguationData":[TD([[makeQuery(id+"F0.imprint","INTERSECT",VERTEX,{"derivedFrom":[subQ0,sQuery(id+"F0.wireOp",EDGE,"E11.MirrorC")]}),1.0]])],"derivedFrom":subQ0})])],"isStart":false});}
            fillet(context, id + "F12", {"entities" : qUnion([Q0, Q1, Q2, Q3, Q4, Q5, Q6, Q7, Q8, Q9, Q10, Q11, Q12, Q13, Q14, Q15, Q16, Q17, Q18, Q19, Q20]), "radius" : 1.59 * mm, "tangentPropagation" : true, "allowEdgeOverflow" : false});
        }
    });
